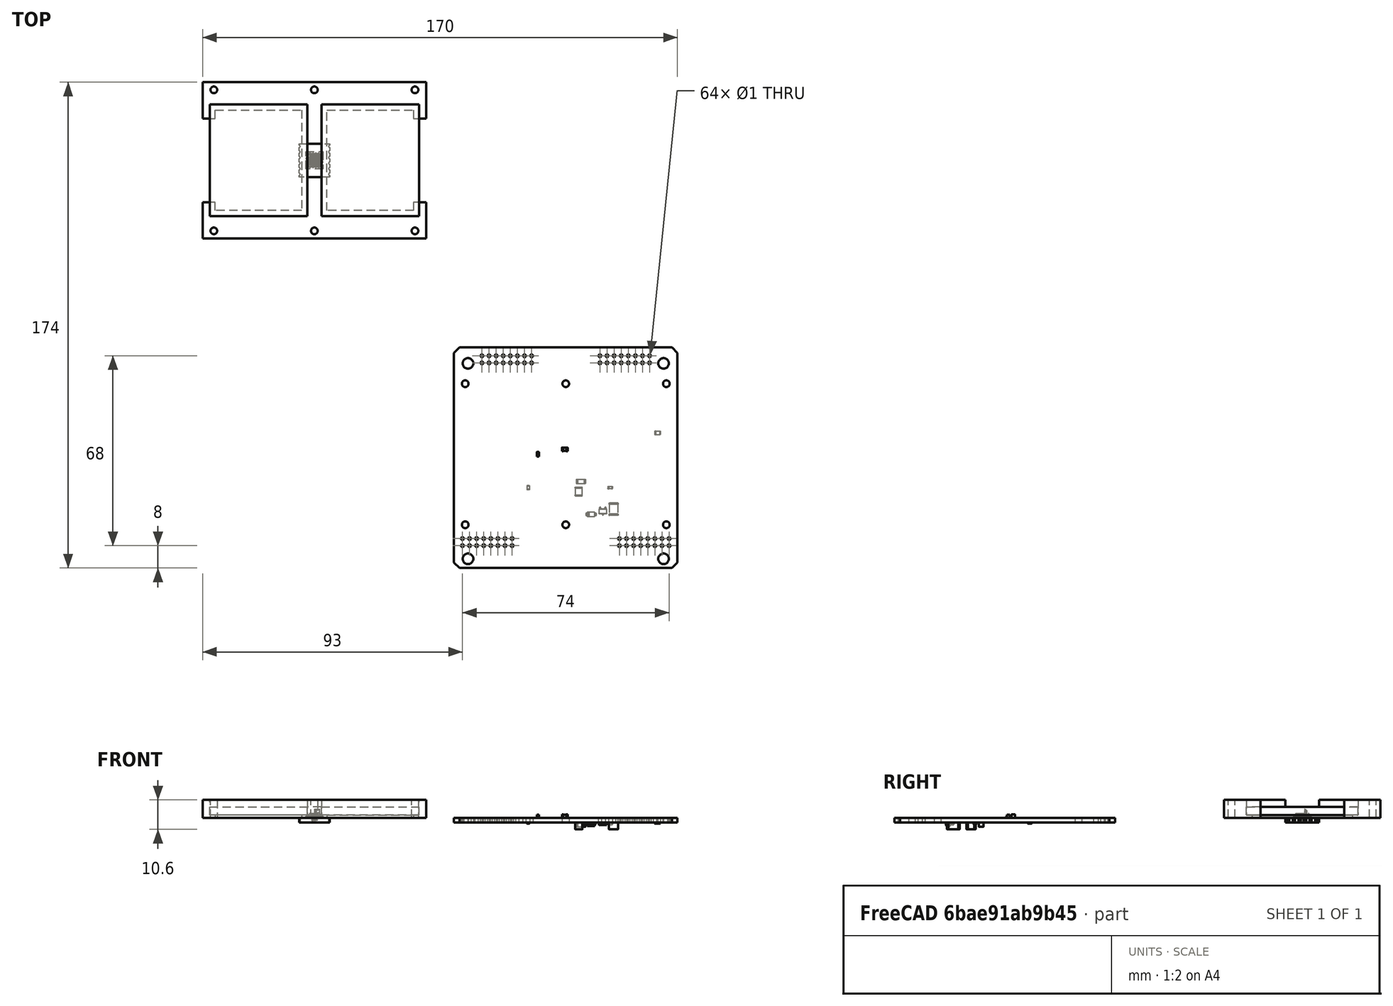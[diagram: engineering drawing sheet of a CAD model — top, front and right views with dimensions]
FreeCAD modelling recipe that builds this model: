
FCSTD DOCUMENT  (FreeCAD 0.21R33771 (Git))
Label: PlacaCarcasaV3
License: All rights reserved
LicenseURL: http://en.wikipedia.org/wiki/All_rights_reserved
objects: Part::Feature×268, App::Link×148, App::Part×28, PartDesign::CoordinateSystem×1, Sketcher::SketchObject×1
note: 270 computed .brp shape members not serialized (recipe doc carries the construction recipe); baked Part::Feature solids carry a one-line shape summary decoded from their .brp

FEATURE [PartDesign::CoordinateSystem] Local_CS_d980
  AttacherType = Attacher::AttachEngine3D
  MapMode = 2
  Support = -> [X_Axis001]
FEATURE [Part::Feature] Pcb_d980
  shape: bbox 80 x 79 x 1.6 mm, 84 faces (baked)
FEATURE [Sketcher::SketchObject] PCB_Sketch_d980
  FullyConstrained = false
  sketch-geometry (12):
    g0: LineSegment StartX=52 StartY=-146 StartZ=0 EndX=50 EndY=-144 EndZ=0
    g1: LineSegment StartX=50 StartY=-69 StartZ=0 EndX=52 EndY=-67 EndZ=0
    g2: LineSegment StartX=50 StartY=-144 StartZ=0 EndX=50 EndY=-69 EndZ=0
    g3: LineSegment StartX=52 StartY=-67 StartZ=0 EndX=128 EndY=-67 EndZ=0
    g4: LineSegment StartX=128 StartY=-146 StartZ=0 EndX=52 EndY=-146 EndZ=0
    g5: LineSegment StartX=128 StartY=-67 StartZ=0 EndX=130 EndY=-69 EndZ=0
    g6: LineSegment StartX=130 StartY=-69 StartZ=0 EndX=130 EndY=-144 EndZ=0
    g7: LineSegment StartX=130 StartY=-144 StartZ=0 EndX=128 EndY=-146 EndZ=0
    g8: Circle CenterX=125 CenterY=-142.7 CenterZ=0 NormalX=0 NormalY=0 NormalZ=1 AngleXU=0 Radius=1.9
    g9: Circle CenterX=55 CenterY=-72.7 CenterZ=0 NormalX=0 NormalY=0 NormalZ=1 AngleXU=0 Radius=1.9
    g10: Circle CenterX=55 CenterY=-142.7 CenterZ=0 NormalX=0 NormalY=0 NormalZ=1 AngleXU=0 Radius=1.9
    g11: Circle CenterX=125 CenterY=-72.7 CenterZ=0 NormalX=0 NormalY=0 NormalZ=1 AngleXU=0 Radius=1.9
  constraints (8):
    c: Coincident(g0,g2)
    c: Coincident(g1,g2)
    c: Coincident(g0,g4)
    c: Coincident(g1,g3)
    c: Coincident(g4,g7)
    c: Coincident(g3,g5)
    c: Coincident(g6,g7)
    c: Coincident(g5,g6)
FEATURE [Part::Feature] Part__Feature  label="BODY-SOT"
  Placement = pos=(0,0,0.9) rot=(0.57735,-0.57735,-0.57735;2.0944rad)
  shape: bbox 1.6 x 2.9 x 1.1 mm, 42 faces (baked)
FEATURE [Part::Feature] Part__Feature001  label="LEAD-SOT"
  Placement = pos=(-0.939537,-0.95,0.25) rot=(0.57735,-0.57735,-0.57735;2.0944rad)
  shape: bbox 0.6 x 0.4 x 0.9 mm, 14 faces (baked)
FEATURE [Part::Feature] Part__Feature002  label="LEAD-SOT001"
  Placement = pos=(-0.939537,0,0.25) rot=(0.57735,-0.57735,-0.57735;2.0944rad)
  shape: bbox 0.6 x 0.4 x 0.9 mm, 14 faces (baked)
FEATURE [Part::Feature] Part__Feature003  label="LEAD-SOT002"
  Placement = pos=(-0.939537,0.95,0.25) rot=(0.57735,-0.57735,-0.57735;2.0944rad)
  shape: bbox 0.6 x 0.4 x 0.9 mm, 14 faces (baked)
FEATURE [Part::Feature] Part__Feature004  label="LEAD-SOT003"
  Placement = pos=(0.939537,-0.95,0.25) rot=(0.57735,0.57735,0.57735;2.0944rad)
  shape: bbox 0.6 x 0.4 x 0.9 mm, 14 faces (baked)
FEATURE [Part::Feature] Part__Feature005  label="LEAD-SOT004"
  Placement = pos=(0.939537,0,0.25) rot=(0.57735,0.57735,0.57735;2.0944rad)
  shape: bbox 0.6 x 0.4 x 0.9 mm, 14 faces (baked)
FEATURE [Part::Feature] Part__Feature006  label="LEAD-SOT005"
  Placement = pos=(0.939537,0.95,0.25) rot=(0.57735,0.57735,0.57735;2.0944rad)
  shape: bbox 0.6 x 0.4 x 0.9 mm, 14 faces (baked)
FEATURE [App::Part] DBV0006A_ASM  label="07_SensorTemperatura.kicad_sch_DBV0006A_ASM_bef77850255a"
  Group = -> [Part__Feature,Part__Feature001,Part__Feature002,Part__Feature003,Part__Feature004,Part__Feature005,Part__Feature006]
  Origin = -> Origin008
  Placement = pos=(89.6348,-106.35,0) rot=(0,0,1;3.14159rad)
FEATURE [Part::Feature] Shape  label="06_PlacasSiPM.kicad_sch_LED_0603_1608Metric_667c60cf1737"
  Placement = pos=(80,-105.25,0) rot=(0,0,-1;1.5708rad)
  shape: bbox 0.8 x 1.6 x 1.1 mm, 50 faces (baked)
FEATURE [Part::Feature] Shape001  label="07_SensorTemperatura.kicad_sch_C_0805_2012Metric_4f3bec8a4ad3"
  Placement = pos=(89.65,-103.5,0) rot=(0,0,1;0rad)
  shape: bbox 2 x 1.25 x 1.25 mm, 28 faces (baked)
FEATURE [Part::Feature] Part__Feature007  label="Cuerpo"
  shape: bbox 80 x 56 x 6.5 mm, 44 faces (baked)
FEATURE [Part::Feature] Part__Feature008  label="Extrude"
  Placement = pos=(20,0,1) rot=(0,0,1;0rad)
  shape: bbox 35 x 40 x 3 mm, 6 faces (baked)
FEATURE [Part::Feature] Part__Feature009  label="Extrude001"
  Placement = pos=(-20,0,1) rot=(0,0,1;0rad)
  shape: bbox 35 x 40 x 3 mm, 6 faces (baked)
FEATURE [App::Part] CarcasaV3  label="06_PlacasSiPM.kicad_sch_CarcasaV3_ad8b2182f1ab"
  Group = -> [Part__Feature007,Part__Feature008,Part__Feature009]
  Origin = -> Origin009
  Placement = pos=(90,-105.25,6.5) rot=(1,0,0;3.14159rad)
FEATURE [App::Link] _6_PlacasSiPM_kicad_sch_LED_0603_1608Metric_667c60cf1737_ln_  label="06_PlacasSiPM.kicad_sch_PlacasSiPM.kicad_sch_LED_0603_1608Metric_7981f1ddc297"
  LinkPlacement = pos=(100,-105.25,0) rot=(0,0,-1;1.5708rad)
  LinkedObject = -> Shape
  Placement = pos=(100,-105.25,0) rot=(0,0,-1;1.5708rad)
FEATURE [Part::Feature] Part__Feature010  label="Pcb_1cf2"
  Placement = pos=(-150.5,123,0) rot=(0,0,1;0rad)
  shape: bbox 11 x 12 x 1.6 mm, 36 faces (baked)
FEATURE [Part::Feature] Part__Feature011  label="topPads_1cf2_cut"
  Placement = pos=(0,0,0.02) rot=(0,0,1;0rad)
  shape: bbox 0.675 x 1.35 x 2e-07 mm, 1 faces, 0 solids (baked)
FEATURE [Part::Feature] Part__Feature012  label="topPads_1cf2_cut001"
  Placement = pos=(0,0,0.02) rot=(0,0,1;0rad)
  shape: bbox 0.675 x 1.35 x 2e-07 mm, 1 faces, 0 solids (baked)
FEATURE [Part::Feature] Part__Feature013  label="topPads_1cf2_cut002"
  Placement = pos=(0,0,0.02) rot=(0,0,1;0rad)
  shape: bbox 0.675 x 1.35 x 2e-07 mm, 1 faces, 0 solids (baked)
FEATURE [Part::Feature] Part__Feature014  label="topPads_1cf2_cut003"
  Placement = pos=(0,0,0.02) rot=(0,0,1;0rad)
  shape: bbox 0.675 x 1.35 x 2e-07 mm, 1 faces, 0 solids (baked)
FEATURE [Part::Feature] Part__Feature015  label="topPads_1cf2_cut004"
  Placement = pos=(0,0,0.02) rot=(0,0,1;0rad)
  shape: bbox 0.675 x 1.35 x 2e-07 mm, 1 faces, 0 solids (baked)
FEATURE [Part::Feature] Part__Feature016  label="topPads_1cf2_cut005"
  Placement = pos=(0,0,0.02) rot=(0,0,1;0rad)
  shape: bbox 0.675 x 1.35 x 2e-07 mm, 1 faces, 0 solids (baked)
FEATURE [Part::Feature] Part__Feature017  label="topPads_1cf2_cut006"
  Placement = pos=(0,0,0.02) rot=(0,0,1;0rad)
  shape: bbox 0.675 x 1.35 x 2e-07 mm, 1 faces, 0 solids (baked)
FEATURE [Part::Feature] Part__Feature018  label="topPads_1cf2_cut007"
  Placement = pos=(0,0,0.02) rot=(0,0,1;0rad)
  shape: bbox 0.675 x 1.35 x 2e-07 mm, 1 faces, 0 solids (baked)
FEATURE [Part::Feature] Part__Feature019  label="topPads_1cf2_cut008"
  Placement = pos=(0,0,0.02) rot=(0,0,1;0rad)
  shape: bbox 0.675 x 1.35 x 2e-07 mm, 1 faces, 0 solids (baked)
FEATURE [Part::Feature] Part__Feature020  label="topPads_1cf2_cut009"
  Placement = pos=(0,0,0.02) rot=(0,0,1;0rad)
  shape: bbox 0.675 x 1.35 x 2e-07 mm, 1 faces, 0 solids (baked)
FEATURE [Part::Feature] Part__Feature021  label="topPads_1cf2_cut010"
  Placement = pos=(0,0,0.02) rot=(0,0,1;0rad)
  shape: bbox 0.675 x 1.35 x 2e-07 mm, 1 faces, 0 solids (baked)
FEATURE [Part::Feature] Part__Feature022  label="topPads_1cf2_cut011"
  Placement = pos=(0,0,0.02) rot=(0,0,1;0rad)
  shape: bbox 0.675 x 1.35 x 2e-07 mm, 1 faces, 0 solids (baked)
FEATURE [Part::Feature] Part__Feature023  label="topPads_1cf2_cut012"
  Placement = pos=(0,0,0.02) rot=(0,0,1;0rad)
  shape: bbox 0.6 x 0.6 x 2e-07 mm, 1 faces, 0 solids (baked)
FEATURE [Part::Feature] Part__Feature024  label="topPads_1cf2_cut013"
  Placement = pos=(0,0,0.02) rot=(0,0,1;0rad)
  shape: bbox 0.6 x 0.6 x 2e-07 mm, 1 faces, 0 solids (baked)
FEATURE [Part::Feature] Part__Feature025  label="topPads_1cf2_cut014"
  Placement = pos=(0,0,0.02) rot=(0,0,1;0rad)
  shape: bbox 0.6 x 0.6 x 2e-07 mm, 1 faces, 0 solids (baked)
FEATURE [Part::Feature] Part__Feature026  label="topPads_1cf2_cut015"
  Placement = pos=(0,0,0.02) rot=(0,0,1;0rad)
  shape: bbox 0.6 x 0.6 x 2e-07 mm, 1 faces, 0 solids (baked)
FEATURE [Part::Feature] Part__Feature027  label="topPads_1cf2_cut016"
  Placement = pos=(0,0,0.02) rot=(0,0,1;0rad)
  shape: bbox 0.6 x 0.6 x 2e-07 mm, 1 faces, 0 solids (baked)
FEATURE [Part::Feature] Part__Feature028  label="topPads_1cf2_cut017"
  Placement = pos=(0,0,0.02) rot=(0,0,1;0rad)
  shape: bbox 0.6 x 0.6 x 2e-07 mm, 1 faces, 0 solids (baked)
FEATURE [Part::Feature] Part__Feature029  label="topPads_1cf2_cut018"
  Placement = pos=(0,0,0.02) rot=(0,0,1;0rad)
  shape: bbox 0.2032 x 0.2032 x 2e-07 mm, 1 faces, 0 solids (baked)
FEATURE [Part::Feature] Part__Feature030  label="topPads_1cf2_cut019"
  Placement = pos=(0,0,0.02) rot=(0,0,1;0rad)
  shape: bbox 0.2032 x 0.2032 x 2e-07 mm, 1 faces, 0 solids (baked)
FEATURE [Part::Feature] Part__Feature031  label="topPads_1cf2_cut020"
  Placement = pos=(0,0,0.02) rot=(0,0,1;0rad)
  shape: bbox 0.2032 x 0.2032 x 2e-07 mm, 1 faces, 0 solids (baked)
FEATURE [Part::Feature] Part__Feature032  label="topPads_1cf2_cut021"
  Placement = pos=(0,0,0.02) rot=(0,0,1;0rad)
  shape: bbox 0.2032 x 0.2032 x 2e-07 mm, 1 faces, 0 solids (baked)
FEATURE [Part::Feature] Part__Feature033  label="topPads_1cf2_cut022"
  Placement = pos=(0,0,0.02) rot=(0,0,1;0rad)
  shape: bbox 0.2032 x 0.2032 x 2e-07 mm, 1 faces, 0 solids (baked)
FEATURE [Part::Feature] Part__Feature034  label="topPads_1cf2_cut023"
  Placement = pos=(0,0,0.02) rot=(0,0,1;0rad)
  shape: bbox 0.2032 x 0.2032 x 2e-07 mm, 1 faces, 0 solids (baked)
FEATURE [Part::Feature] Part__Feature035  label="topPads_1cf2_cut024"
  Placement = pos=(0,0,0.02) rot=(0,0,1;0rad)
  shape: bbox 0.2032 x 0.2032 x 2e-07 mm, 1 faces, 0 solids (baked)
FEATURE [Part::Feature] Part__Feature036  label="topPads_1cf2_cut025"
  Placement = pos=(0,0,0.02) rot=(0,0,1;0rad)
  shape: bbox 0.2032 x 0.2032 x 2e-07 mm, 1 faces, 0 solids (baked)
FEATURE [Part::Feature] Part__Feature037  label="topPads_1cf2_cut026"
  Placement = pos=(0,0,0.02) rot=(0,0,1;0rad)
  shape: bbox 0.2032 x 0.2032 x 2e-07 mm, 1 faces, 0 solids (baked)
FEATURE [Part::Feature] Part__Feature038  label="topPads_1cf2_cut027"
  Placement = pos=(0,0,0.02) rot=(0,0,1;0rad)
  shape: bbox 0.2032 x 0.2032 x 2e-07 mm, 1 faces, 0 solids (baked)
FEATURE [Part::Feature] Part__Feature039  label="topPads_1cf2_cut028"
  Placement = pos=(0,0,0.02) rot=(0,0,1;0rad)
  shape: bbox 0.2032 x 0.2032 x 2e-07 mm, 1 faces, 0 solids (baked)
FEATURE [Part::Feature] Part__Feature040  label="topPads_1cf2_cut029"
  Placement = pos=(0,0,0.02) rot=(0,0,1;0rad)
  shape: bbox 0.2032 x 0.2032 x 2e-07 mm, 1 faces, 0 solids (baked)
FEATURE [Part::Feature] Part__Feature041  label="topPads_1cf2_cut030"
  Placement = pos=(0,0,0.02) rot=(0,0,1;0rad)
  shape: bbox 0.2032 x 0.2032 x 2e-07 mm, 1 faces, 0 solids (baked)
FEATURE [Part::Feature] Part__Feature042  label="topPads_1cf2_cut031"
  Placement = pos=(0,0,0.02) rot=(0,0,1;0rad)
  shape: bbox 0.2032 x 0.2032 x 2e-07 mm, 1 faces, 0 solids (baked)
FEATURE [Part::Feature] Part__Feature043  label="topPads_1cf2_cut032"
  Placement = pos=(0,0,0.02) rot=(0,0,1;0rad)
  shape: bbox 0.2032 x 0.2032 x 2e-07 mm, 1 faces, 0 solids (baked)
FEATURE [Part::Feature] Part__Feature044  label="topPads_1cf2_cut033"
  Placement = pos=(0,0,0.02) rot=(0,0,1;0rad)
  shape: bbox 0.2032 x 0.2032 x 2e-07 mm, 1 faces, 0 solids (baked)
FEATURE [Part::Feature] Part__Feature045  label="topPads_1cf2_cut034"
  Placement = pos=(0,0,0.02) rot=(0,0,1;0rad)
  shape: bbox 0.2032 x 0.2032 x 2e-07 mm, 1 faces, 0 solids (baked)
FEATURE [Part::Feature] Part__Feature046  label="topPads_1cf2_cut035"
  Placement = pos=(0,0,0.02) rot=(0,0,1;0rad)
  shape: bbox 0.2032 x 0.2032 x 2e-07 mm, 1 faces, 0 solids (baked)
FEATURE [Part::Feature] Part__Feature047  label="topPads_1cf2_cut036"
  Placement = pos=(0,0,0.02) rot=(0,0,1;0rad)
  shape: bbox 0.2032 x 0.2032 x 2e-07 mm, 1 faces, 0 solids (baked)
FEATURE [Part::Feature] Part__Feature048  label="topPads_1cf2_cut037"
  Placement = pos=(0,0,0.02) rot=(0,0,1;0rad)
  shape: bbox 0.2032 x 0.2032 x 2e-07 mm, 1 faces, 0 solids (baked)
FEATURE [Part::Feature] Part__Feature049  label="topPads_1cf2_cut038"
  Placement = pos=(0,0,0.02) rot=(0,0,1;0rad)
  shape: bbox 0.2032 x 0.2032 x 2e-07 mm, 1 faces, 0 solids (baked)
FEATURE [Part::Feature] Part__Feature050  label="topPads_1cf2_cut039"
  Placement = pos=(0,0,0.02) rot=(0,0,1;0rad)
  shape: bbox 0.2032 x 0.2032 x 2e-07 mm, 1 faces, 0 solids (baked)
FEATURE [Part::Feature] Part__Feature051  label="topPads_1cf2_cut040"
  Placement = pos=(0,0,0.02) rot=(0,0,1;0rad)
  shape: bbox 0.2032 x 0.2032 x 2e-07 mm, 1 faces, 0 solids (baked)
FEATURE [Part::Feature] Part__Feature052  label="topPads_1cf2_cut041"
  Placement = pos=(0,0,0.02) rot=(0,0,1;0rad)
  shape: bbox 0.2032 x 0.2032 x 2e-07 mm, 1 faces, 0 solids (baked)
FEATURE [Part::Feature] Part__Feature053  label="topPads_1cf2_cut042"
  Placement = pos=(0,0,0.02) rot=(0,0,1;0rad)
  shape: bbox 0.2032 x 0.2032 x 2e-07 mm, 1 faces, 0 solids (baked)
FEATURE [Part::Feature] Part__Feature054  label="topPads_1cf2_cut043"
  Placement = pos=(0,0,0.02) rot=(0,0,1;0rad)
  shape: bbox 0.2032 x 0.2032 x 2e-07 mm, 1 faces, 0 solids (baked)
FEATURE [Part::Feature] Part__Feature055  label="topPads_1cf2_cut044"
  Placement = pos=(0,0,0.02) rot=(0,0,1;0rad)
  shape: bbox 0.2032 x 0.2032 x 2e-07 mm, 1 faces, 0 solids (baked)
FEATURE [Part::Feature] Part__Feature056  label="topPads_1cf2_cut045"
  Placement = pos=(0,0,0.02) rot=(0,0,1;0rad)
  shape: bbox 0.2032 x 0.2032 x 2e-07 mm, 1 faces, 0 solids (baked)
FEATURE [Part::Feature] Part__Feature057  label="topPads_1cf2_cut046"
  Placement = pos=(0,0,0.02) rot=(0,0,1;0rad)
  shape: bbox 0.2032 x 0.2032 x 2e-07 mm, 1 faces, 0 solids (baked)
FEATURE [Part::Feature] Part__Feature058  label="topPads_1cf2_cut047"
  Placement = pos=(0,0,0.02) rot=(0,0,1;0rad)
  shape: bbox 0.2032 x 0.2032 x 2e-07 mm, 1 faces, 0 solids (baked)
FEATURE [Part::Feature] Part__Feature059  label="topPads_1cf2_cut048"
  Placement = pos=(0,0,0.02) rot=(0,0,1;0rad)
  shape: bbox 0.2032 x 0.2032 x 2e-07 mm, 1 faces, 0 solids (baked)
FEATURE [Part::Feature] Part__Feature060  label="topPads_1cf2_cut049"
  Placement = pos=(0,0,0.02) rot=(0,0,1;0rad)
  shape: bbox 0.2032 x 0.2032 x 2e-07 mm, 1 faces, 0 solids (baked)
FEATURE [Part::Feature] Part__Feature061  label="topPads_1cf2_cut050"
  Placement = pos=(0,0,0.02) rot=(0,0,1;0rad)
  shape: bbox 0.2032 x 0.2032 x 2e-07 mm, 1 faces, 0 solids (baked)
FEATURE [Part::Feature] Part__Feature062  label="topPads_1cf2_cut051"
  Placement = pos=(0,0,0.02) rot=(0,0,1;0rad)
  shape: bbox 0.2032 x 0.2032 x 2e-07 mm, 1 faces, 0 solids (baked)
FEATURE [Part::Feature] Part__Feature063  label="topPads_1cf2_cut052"
  Placement = pos=(0,0,0.02) rot=(0,0,1;0rad)
  shape: bbox 0.2032 x 0.2032 x 2e-07 mm, 1 faces, 0 solids (baked)
FEATURE [Part::Feature] Part__Feature064  label="topPads_1cf2_cut053"
  Placement = pos=(0,0,0.02) rot=(0,0,1;0rad)
  shape: bbox 0.2032 x 0.2032 x 2e-07 mm, 1 faces, 0 solids (baked)
FEATURE [App::Part] topPads_1cf2_cut  label="topPads_1cf2_cut054"
  Group = -> [Part__Feature011,Part__Feature012,Part__Feature013,Part__Feature014,Part__Feature015,Part__Feature016,Part__Feature017,Part__Feature018,Part__Feature019,Part__Feature020,Part__Feature021,Part__Feature022,Part__Feature023,Part__Feature024,Part__Feature025,Part__Feature026,Part__Feature027,Part__Feature028,Part__Feature029,Part__Feature030,Part__Feature031,Part__Feature032,Part__Feature033,+31 more]
  Origin = -> Origin010
FEATURE [Part::Feature] Part__Feature065  label="topTracks_1cf2"
  Placement = pos=(-150.5,123,0.01) rot=(0,0,1;0rad)
  shape: bbox 0.8 x 2.3 x 2e-07 mm, 1 faces, 0 solids (baked)
FEATURE [Part::Feature] Part__Feature066  label="topTracks_1cf003"
  Placement = pos=(-150.5,123,0.01) rot=(0,0,1;0rad)
  shape: bbox 1.492 x 0.9917 x 2e-07 mm, 1 faces, 0 solids (baked)
FEATURE [Part::Feature] Part__Feature067  label="topTracks_1cf004"
  Placement = pos=(-150.5,123,0.01) rot=(0,0,1;0rad)
  shape: bbox 1.492 x 0.9917 x 2e-07 mm, 1 faces, 0 solids (baked)
FEATURE [Part::Feature] Part__Feature068  label="topTracks_1cf005"
  Placement = pos=(-150.5,123,0.01) rot=(0,0,1;0rad)
  shape: bbox 0.6917 x 1.592 x 2e-07 mm, 1 faces, 0 solids (baked)
FEATURE [Part::Feature] Part__Feature069  label="topTracks_1cf006"
  Placement = pos=(-150.5,123,0.01) rot=(0,0,1;0rad)
  shape: bbox 1.492 x 0.5917 x 2e-07 mm, 1 faces, 0 solids (baked)
FEATURE [Part::Feature] Part__Feature070  label="topTracks_1cf007"
  Placement = pos=(-150.5,123,0.01) rot=(0,0,1;0rad)
  shape: bbox 1.492 x 0.5917 x 2e-07 mm, 1 faces, 0 solids (baked)
FEATURE [Part::Feature] Part__Feature071  label="topTracks_1cf008"
  Placement = pos=(-150.5,123,0.01) rot=(0,0,1;0rad)
  shape: bbox 0.1969 x 0.1969 x 2e-07 mm, 1 faces, 0 solids (baked)
FEATURE [App::Part] topTracks_1cf2  label="topTracks_1cf009"
  Group = -> [Part__Feature065,Part__Feature066,Part__Feature067,Part__Feature068,Part__Feature069,Part__Feature070,Part__Feature071]
  Origin = -> Origin011
FEATURE [Part::Feature] Part__Feature072  label="topZones_1cf2"
  Placement = pos=(-150.5,123,0.01) rot=(0,0,1;0rad)
  shape: bbox 10.7 x 12.05 x 2e-07 mm, 1 faces, 0 solids (baked)
FEATURE [Part::Feature] Part__Feature073  label="botPads_1cf2_cut"
  Placement = pos=(0,0,-1.62) rot=(0,0,1;0rad)
  shape: bbox 0.675 x 1.35 x 2e-07 mm, 1 faces, 0 solids (baked)
FEATURE [Part::Feature] Part__Feature074  label="botPads_1cf2_cut001"
  Placement = pos=(0,0,-1.62) rot=(0,0,1;0rad)
  shape: bbox 0.675 x 1.35 x 2e-07 mm, 1 faces, 0 solids (baked)
FEATURE [Part::Feature] Part__Feature075  label="botPads_1cf2_cut002"
  Placement = pos=(0,0,-1.62) rot=(0,0,1;0rad)
  shape: bbox 0.675 x 1.35 x 2e-07 mm, 1 faces, 0 solids (baked)
FEATURE [Part::Feature] Part__Feature076  label="botPads_1cf2_cut003"
  Placement = pos=(0,0,-1.62) rot=(0,0,1;0rad)
  shape: bbox 0.675 x 1.35 x 2e-07 mm, 1 faces, 0 solids (baked)
FEATURE [Part::Feature] Part__Feature077  label="botPads_1cf2_cut004"
  Placement = pos=(0,0,-1.62) rot=(0,0,1;0rad)
  shape: bbox 0.675 x 1.35 x 2e-07 mm, 1 faces, 0 solids (baked)
FEATURE [Part::Feature] Part__Feature078  label="botPads_1cf2_cut005"
  Placement = pos=(0,0,-1.62) rot=(0,0,1;0rad)
  shape: bbox 0.675 x 1.35 x 2e-07 mm, 1 faces, 0 solids (baked)
FEATURE [Part::Feature] Part__Feature079  label="botPads_1cf2_cut006"
  Placement = pos=(0,0,-1.62) rot=(0,0,1;0rad)
  shape: bbox 0.675 x 1.35 x 2e-07 mm, 1 faces, 0 solids (baked)
FEATURE [Part::Feature] Part__Feature080  label="botPads_1cf2_cut007"
  Placement = pos=(0,0,-1.62) rot=(0,0,1;0rad)
  shape: bbox 0.675 x 1.35 x 2e-07 mm, 1 faces, 0 solids (baked)
FEATURE [Part::Feature] Part__Feature081  label="botPads_1cf2_cut008"
  Placement = pos=(0,0,-1.62) rot=(0,0,1;0rad)
  shape: bbox 0.675 x 1.35 x 2e-07 mm, 1 faces, 0 solids (baked)
FEATURE [Part::Feature] Part__Feature082  label="botPads_1cf2_cut009"
  Placement = pos=(0,0,-1.62) rot=(0,0,1;0rad)
  shape: bbox 0.675 x 1.35 x 2e-07 mm, 1 faces, 0 solids (baked)
FEATURE [Part::Feature] Part__Feature083  label="botPads_1cf2_cut010"
  Placement = pos=(0,0,-1.62) rot=(0,0,1;0rad)
  shape: bbox 0.675 x 1.35 x 2e-07 mm, 1 faces, 0 solids (baked)
FEATURE [Part::Feature] Part__Feature084  label="botPads_1cf2_cut011"
  Placement = pos=(0,0,-1.62) rot=(0,0,1;0rad)
  shape: bbox 0.675 x 1.35 x 2e-07 mm, 1 faces, 0 solids (baked)
FEATURE [Part::Feature] Part__Feature085  label="botPads_1cf2_cut012"
  Placement = pos=(0,0,-1.62) rot=(0,0,1;0rad)
  shape: bbox 0.6 x 0.6 x 2e-07 mm, 1 faces, 0 solids (baked)
FEATURE [Part::Feature] Part__Feature086  label="botPads_1cf2_cut013"
  Placement = pos=(0,0,-1.62) rot=(0,0,1;0rad)
  shape: bbox 0.6 x 0.6 x 2e-07 mm, 1 faces, 0 solids (baked)
FEATURE [Part::Feature] Part__Feature087  label="botPads_1cf2_cut014"
  Placement = pos=(0,0,-1.62) rot=(0,0,1;0rad)
  shape: bbox 0.6 x 0.6 x 2e-07 mm, 1 faces, 0 solids (baked)
FEATURE [Part::Feature] Part__Feature088  label="botPads_1cf2_cut015"
  Placement = pos=(0,0,-1.62) rot=(0,0,1;0rad)
  shape: bbox 0.6 x 0.6 x 2e-07 mm, 1 faces, 0 solids (baked)
FEATURE [Part::Feature] Part__Feature089  label="botPads_1cf2_cut016"
  Placement = pos=(0,0,-1.62) rot=(0,0,1;0rad)
  shape: bbox 0.6 x 0.6 x 2e-07 mm, 1 faces, 0 solids (baked)
FEATURE [Part::Feature] Part__Feature090  label="botPads_1cf2_cut017"
  Placement = pos=(0,0,-1.62) rot=(0,0,1;0rad)
  shape: bbox 0.6 x 0.6 x 2e-07 mm, 1 faces, 0 solids (baked)
FEATURE [App::Part] botPads_1cf2_cut  label="botPads_1cf2_cut018"
  Group = -> [Part__Feature073,Part__Feature074,Part__Feature075,Part__Feature076,Part__Feature077,Part__Feature078,Part__Feature079,Part__Feature080,Part__Feature081,Part__Feature082,Part__Feature083,Part__Feature084,Part__Feature085,Part__Feature086,Part__Feature087,Part__Feature088,Part__Feature089,Part__Feature090]
  Origin = -> Origin012
FEATURE [Part::Feature] Part__Feature091  label="botTracks_1cf2"
  Placement = pos=(-150.5,123,-1.61) rot=(0,0,1;0rad)
  shape: bbox 9.113 x 5.6 x 2e-07 mm, 1 faces, 0 solids (baked)
FEATURE [Part::Feature] Part__Feature092  label="botTracks_1cf003"
  Placement = pos=(-150.5,123,-1.61) rot=(0,0,1;0rad)
  shape: bbox 1.297 x 3.297 x 2e-07 mm, 1 faces, 0 solids (baked)
FEATURE [App::Part] botTracks_1cf2  label="botTracks_1cf004"
  Group = -> [Part__Feature091,Part__Feature092]
  Origin = -> Origin013
FEATURE [App::Part] Board_Geoms_1cf2
  Group = -> [Part__Feature010,topPads_1cf2_cut,topTracks_1cf2,Part__Feature072,botPads_1cf2_cut,botTracks_1cf2]
  Origin = -> Origin014
FEATURE [Part::Feature] Part__Feature093  label="part"
  shape: bbox 0.254 x 0.254 x 0.254 mm, 1 faces (baked)
FEATURE [Part::Feature] Part__Feature094  label="part001"
  shape: bbox 0.254 x 0.254 x 0.254 mm, 1 faces (baked)
FEATURE [Part::Feature] Part__Feature095  label="part002"
  shape: bbox 0.254 x 0.254 x 0.254 mm, 1 faces (baked)
FEATURE [Part::Feature] Part__Feature096  label="part003"
  shape: bbox 0.254 x 0.254 x 0.254 mm, 1 faces (baked)
FEATURE [Part::Feature] Part__Feature097  label="part004"
  shape: bbox 0.254 x 0.254 x 0.254 mm, 1 faces (baked)
FEATURE [Part::Feature] Part__Feature098  label="part005"
  shape: bbox 0.254 x 0.254 x 0.254 mm, 1 faces (baked)
FEATURE [Part::Feature] Part__Feature099  label="part006"
  shape: bbox 0.254 x 0.254 x 0.254 mm, 1 faces (baked)
FEATURE [Part::Feature] Part__Feature100  label="part007"
  shape: bbox 0.254 x 0.254 x 0.254 mm, 1 faces (baked)
FEATURE [Part::Feature] Part__Feature101  label="part008"
  shape: bbox 0.254 x 0.254 x 0.254 mm, 1 faces (baked)
FEATURE [Part::Feature] Part__Feature102  label="part009"
  shape: bbox 0.254 x 0.254 x 0.254 mm, 1 faces (baked)
FEATURE [Part::Feature] Part__Feature103  label="part010"
  shape: bbox 0.254 x 0.254 x 0.254 mm, 1 faces (baked)
FEATURE [Part::Feature] Part__Feature104  label="part011"
  shape: bbox 0.254 x 0.254 x 0.254 mm, 1 faces (baked)
FEATURE [Part::Feature] Part__Feature105  label="part012"
  shape: bbox 0.254 x 0.254 x 0.254 mm, 1 faces (baked)
FEATURE [Part::Feature] Part__Feature106  label="part013"
  shape: bbox 0.254 x 0.254 x 0.254 mm, 1 faces (baked)
FEATURE [Part::Feature] Part__Feature107  label="part014"
  shape: bbox 0.254 x 0.254 x 0.254 mm, 1 faces (baked)
FEATURE [Part::Feature] Part__Feature108  label="part015"
  shape: bbox 0.254 x 0.254 x 0.254 mm, 1 faces (baked)
FEATURE [Part::Feature] Part__Feature109  label="part016"
  shape: bbox 0.254 x 0.254 x 0.254 mm, 1 faces (baked)
FEATURE [Part::Feature] Part__Feature110  label="part017"
  shape: bbox 0.254 x 0.254 x 0.254 mm, 1 faces (baked)
FEATURE [Part::Feature] Part__Feature111  label="part018"
  shape: bbox 0.254 x 0.254 x 0.254 mm, 1 faces (baked)
FEATURE [Part::Feature] Part__Feature112  label="part019"
  shape: bbox 0.254 x 0.254 x 0.254 mm, 1 faces (baked)
FEATURE [Part::Feature] Part__Feature113  label="part020"
  shape: bbox 0.254 x 0.254 x 0.254 mm, 1 faces (baked)
FEATURE [Part::Feature] Part__Feature114  label="part021"
  shape: bbox 0.254 x 0.254 x 0.254 mm, 1 faces (baked)
FEATURE [Part::Feature] Part__Feature115  label="part022"
  shape: bbox 0.254 x 0.254 x 0.254 mm, 1 faces (baked)
FEATURE [Part::Feature] Part__Feature116  label="part023"
  shape: bbox 0.254 x 0.254 x 0.254 mm, 1 faces (baked)
FEATURE [Part::Feature] Part__Feature117  label="part024"
  shape: bbox 0.254 x 0.254 x 0.254 mm, 1 faces (baked)
FEATURE [Part::Feature] Part__Feature118  label="part025"
  shape: bbox 0.254 x 0.254 x 0.254 mm, 1 faces (baked)
FEATURE [Part::Feature] Part__Feature119  label="part026"
  shape: bbox 0.254 x 0.254 x 0.254 mm, 1 faces (baked)
FEATURE [Part::Feature] Part__Feature120  label="part027"
  shape: bbox 0.254 x 0.254 x 0.254 mm, 1 faces (baked)
FEATURE [Part::Feature] Part__Feature121  label="part028"
  shape: bbox 0.254 x 0.254 x 0.254 mm, 1 faces (baked)
FEATURE [Part::Feature] Part__Feature122  label="part029"
  shape: bbox 0.254 x 0.254 x 0.254 mm, 1 faces (baked)
FEATURE [Part::Feature] Part__Feature123  label="part030"
  shape: bbox 0.254 x 0.254 x 0.254 mm, 1 faces (baked)
FEATURE [Part::Feature] Part__Feature124  label="part031"
  shape: bbox 0.254 x 0.254 x 0.254 mm, 1 faces (baked)
FEATURE [Part::Feature] Part__Feature125  label="part032"
  shape: bbox 0.254 x 0.254 x 0.254 mm, 1 faces (baked)
FEATURE [Part::Feature] Part__Feature126  label="part033"
  shape: bbox 0.254 x 0.254 x 0.254 mm, 1 faces (baked)
FEATURE [Part::Feature] Part__Feature127  label="part034"
  shape: bbox 0.254 x 0.254 x 0.254 mm, 1 faces (baked)
FEATURE [Part::Feature] Part__Feature128  label="part035"
  shape: bbox 0.254 x 0.254 x 0.254 mm, 1 faces (baked)
FEATURE [Part::Feature] Part__Feature129  label="part036"
  shape: bbox 0.3086 x 0.3086 x 0.003 mm, 3 faces (baked)
FEATURE [Part::Feature] Part__Feature130  label="part037"
  shape: bbox 6.172 x 6.172 x 0.407 mm, 6 faces (baked)
FEATURE [App::Part] Placa_SiPM_kicad_sch_part038_7e5b207e7f31  label="Placa_SiPM.kicad_sch_part038_7e5b207e7f31"
  Group = -> [Part__Feature093,Part__Feature094,Part__Feature095,Part__Feature096,Part__Feature097,Part__Feature098,Part__Feature099,Part__Feature100,Part__Feature101,Part__Feature102,Part__Feature103,Part__Feature104,Part__Feature105,Part__Feature106,Part__Feature107,Part__Feature108,Part__Feature109,Part__Feature110,Part__Feature111,Part__Feature112,Part__Feature113,Part__Feature114,Part__Feature115,+15 more]
  Origin = -> Origin015
FEATURE [App::Part] Top_1cf2
  Group = -> [Placa_SiPM_kicad_sch_part038_7e5b207e7f31]
  Origin = -> Origin016
FEATURE [App::Part] Step_Models_1cf2
  Group = -> [Top_1cf2]
  Origin = -> Origin017
FEATURE [App::Part] Placa_SiPM  label="06_PlacasSiPM.kicad_sch_Placa_SiPM_8cd53adc4c3a"
  Group = -> [Board_Geoms_1cf2,Step_Models_1cf2]
  Origin = -> Origin018
  Placement = pos=(70,-105.25,1.6) rot=(0,0,1;0rad)
FEATURE [App::Link] _6_PlacasSiPM_kicad_sch_Placa_SiPM_8cd53adc4c3a_ln_  label="06_PlacasSiPM.kicad_sch_PlacasSiPM.kicad_sch_Placa_SiPM_0cbb51f1506e"
  LinkPlacement = pos=(110,-105.25,1.6) rot=(0,0,1;0rad)
  LinkedObject = -> Placa_SiPM
  Placement = pos=(110,-105.25,1.6) rot=(0,0,1;0rad)
FEATURE [App::Part] Top_d980
  Group = -> [DBV0006A_ASM,Shape,Shape001,CarcasaV3,_6_PlacasSiPM_kicad_sch_LED_0603_1608Metric_667c60cf1737_ln_,Placa_SiPM,_6_PlacasSiPM_kicad_sch_Placa_SiPM_8cd53adc4c3a_ln_]
  Origin = -> Origin003
FEATURE [Part::Feature] Shape002  label="01_Polarizacion.kicad_sch_TSOT_23_32137845036f"
  Placement = pos=(103.275,-125.665,-1.6) rot=(0.707107,-0.707107,0;3.14159rad)
  shape: bbox 2.9 x 2.8 x 0.95 mm, 79 faces (baked)
FEATURE [Part::Feature] Shape003  label="04_GenVref.kicad_sch_R_0805_2012Metric_e7e7c0ed52a6"
  Placement = pos=(122.85,-97.568,-1.6) rot=(1,0,0;3.14159rad)
  shape: bbox 2 x 1.2 x 0.45 mm, 26 faces (baked)
FEATURE [Part::Feature] Shape004  label="01_Polarizacion.kicad_sch_R_0603_1608Metric_55dffa615082"
  Placement = pos=(76.525,-117.25,-1.6) rot=(0.707107,-0.707107,0;3.14159rad)
  shape: bbox 0.8 x 1.6 x 0.45 mm, 26 faces (baked)
FEATURE [App::Link] _4_GenVref_kicad_sch_R_0805_2012Metric_e7e7c0ed52a6_ln_  label="03_Comparación.kicad_sch_GenVref.kicad_sch_R_0805_2012Metric_dcaada17983d"
  LinkPlacement = pos=(93.45,-93.75,-1.6) rot=(0.707107,0.707107,0;3.14159rad)
  LinkedObject = -> Shape003
  Placement = pos=(93.45,-93.75,-1.6) rot=(0.707107,0.707107,0;3.14159rad)
FEATURE [Part::Feature] Part__Feature131  label="BODY_MUA08A"
  Placement = pos=(0,0,0.6897) rot=(0.57735,-0.57735,-0.57735;2.0944rad)
  shape: bbox 2.999 x 2.999 x 0.9985 mm, 46 faces (baked)
FEATURE [Part::Feature] Part__Feature132  label="LEAD_MUA08A"
  Placement = pos=(-1.9177,-0.97536,0.254) rot=(0.57735,-0.57735,-0.57735;2.0944rad)
  shape: bbox 0.9525 x 0.3048 x 0.6897 mm, 14 faces (baked)
FEATURE [Part::Feature] Part__Feature133  label="LEAD_MUA08A001"
  Placement = pos=(-1.9177,-0.32512,0.254) rot=(0.57735,-0.57735,-0.57735;2.0944rad)
  shape: bbox 0.9525 x 0.3048 x 0.6897 mm, 14 faces (baked)
FEATURE [Part::Feature] Part__Feature134  label="LEAD_MUA08A002"
  Placement = pos=(-1.9177,0.32512,0.254) rot=(0.57735,-0.57735,-0.57735;2.0944rad)
  shape: bbox 0.9525 x 0.3048 x 0.6897 mm, 14 faces (baked)
FEATURE [Part::Feature] Part__Feature135  label="LEAD_MUA08A003"
  Placement = pos=(-1.9177,0.97536,0.254) rot=(0.57735,-0.57735,-0.57735;2.0944rad)
  shape: bbox 0.9525 x 0.3048 x 0.6897 mm, 14 faces (baked)
FEATURE [Part::Feature] Part__Feature136  label="LEAD_MUA08A004"
  Placement = pos=(1.9177,-0.97536,0.254) rot=(0.57735,0.57735,0.57735;2.0944rad)
  shape: bbox 0.9525 x 0.3048 x 0.6897 mm, 14 faces (baked)
FEATURE [Part::Feature] Part__Feature137  label="LEAD_MUA08A005"
  Placement = pos=(1.9177,-0.32512,0.254) rot=(0.57735,0.57735,0.57735;2.0944rad)
  shape: bbox 0.9525 x 0.3048 x 0.6897 mm, 14 faces (baked)
FEATURE [Part::Feature] Part__Feature138  label="LEAD_MUA08A006"
  Placement = pos=(1.9177,0.32512,0.254) rot=(0.57735,0.57735,0.57735;2.0944rad)
  shape: bbox 0.9525 x 0.3048 x 0.6897 mm, 14 faces (baked)
FEATURE [Part::Feature] Part__Feature139  label="LEAD_MUA08A007"
  Placement = pos=(1.9177,0.97536,0.254) rot=(0.57735,0.57735,0.57735;2.0944rad)
  shape: bbox 0.9525 x 0.3048 x 0.6897 mm, 14 faces (baked)
FEATURE [App::Part] MUA08A_ASM  label="01_Polarizacion.kicad_sch_MUA08A_ASM_555f9891b5ac"
  Group = -> [Part__Feature131,Part__Feature132,Part__Feature133,Part__Feature134,Part__Feature135,Part__Feature136,Part__Feature137,Part__Feature138,Part__Feature139]
  Origin = -> Origin019
  Placement = pos=(78.8633,-134.025,-1.6) rot=(1,0,0;3.14159rad)
FEATURE [Part::Feature] Shape005  label="01_Polarizacion.kicad_sch_C_1206_3216Metric_f1471ee13c61"
  Placement = pos=(95.4,-114.975,-1.6) rot=(1,0,0;3.14159rad)
  shape: bbox 3.2 x 1.6 x 1.6 mm, 28 faces (baked)
FEATURE [App::Link] _7_SensorTemperatura_kicad_sch_C_0805_2012Metric_4f3bec8a4ad3_ln_  label="03_Comparación.kicad_sch_SensorTemperatura.kicad_sch_C_0805_2012Metric_bb25651ed259"
  LinkPlacement = pos=(87.15,-94.5217,-1.6) rot=(0.707107,-0.707107,0;3.14159rad)
  LinkedObject = -> Shape001
  Placement = pos=(87.15,-94.5217,-1.6) rot=(0.707107,-0.707107,0;3.14159rad)
FEATURE [App::Link] _4_GenVref_kicad_sch_R_0805_2012Metric_e7e7c0ed52a6_ln_001  label="01_Polarizacion.kicad_sch_GenVref.kicad_sch_R_0805_2012Metric_055e7035bca4"
  LinkPlacement = pos=(95.65,-133.1,-1.6) rot=(0,1,0;3.14159rad)
  LinkedObject = -> Shape003
  Placement = pos=(95.65,-133.1,-1.6) rot=(0,1,0;3.14159rad)
FEATURE [App::Link] _4_GenVref_kicad_sch_R_0805_2012Metric_e7e7c0ed52a6_ln_002  label="08_MedicionCorriente.kicad_sch_GenVref.kicad_sch_R_0805_2012Metric_8d90b72a5bf4"
  LinkPlacement = pos=(63.3147,-92.6719,-1.6) rot=(0.707107,-0.707107,0;3.14159rad)
  LinkedObject = -> Shape003
  Placement = pos=(63.3147,-92.6719,-1.6) rot=(0.707107,-0.707107,0;3.14159rad)
FEATURE [App::Link] _4_GenVref_kicad_sch_R_0805_2012Metric_e7e7c0ed52a6_ln_003  label="Placa_DetectorParticulas.kicad_sch_GenVref.kicad_sch_R_0805_2012Metric_d41f5b83ae95"
  LinkPlacement = pos=(92.3,-84.95,-1.6) rot=(0.707107,0.707107,0;3.14159rad)
  LinkedObject = -> Shape003
  Placement = pos=(92.3,-84.95,-1.6) rot=(0.707107,0.707107,0;3.14159rad)
FEATURE [App::Link] _7_SensorTemperatura_kicad_sch_C_0805_2012Metric_4f3bec8a4ad3_ln_001  label="01_Polarizacion.kicad_sch_SensorTemperatura.kicad_sch_C_0805_2012Metric_c7f56b1b11b2"
  LinkPlacement = pos=(101.8,-137.1,-1.6) rot=(1,0,0;3.14159rad)
  LinkedObject = -> Shape001
  Placement = pos=(101.8,-137.1,-1.6) rot=(1,0,0;3.14159rad)
FEATURE [Part::Feature] Shape006  label="01_Polarizacion.kicad_sch_D_SOD_123_c84daf4213db"
  Placement = pos=(99.025,-126.775,-1.6) rot=(1,0,0;3.14159rad)
  shape: bbox 3.8 x 1.6 x 1.25 mm, 67 faces (baked)
FEATURE [App::Link] _4_GenVref_kicad_sch_R_0805_2012Metric_e7e7c0ed52a6_ln_004  label="08_MedicionCorriente.kicad_sch_GenVref.kicad_sch_R_0805_2012Metric_9b7ff64fadd9"
  LinkPlacement = pos=(117.375,-91.2,-1.6) rot=(0.707107,0.707107,0;3.14159rad)
  LinkedObject = -> Shape003
  Placement = pos=(117.375,-91.2,-1.6) rot=(0.707107,0.707107,0;3.14159rad)
FEATURE [Part::Feature] Shape007  label="01_Polarizacion.kicad_sch_C_0603_1608Metric_c67edd4d6b6e"
  Placement = pos=(105.9,-117.175,-1.6) rot=(1,0,0;3.14159rad)
  shape: bbox 1.6 x 0.8 x 0.8 mm, 28 faces (baked)
FEATURE [App::Link] _7_SensorTemperatura_kicad_sch_C_0805_2012Metric_4f3bec8a4ad3_ln_002  label="02_Amplificacion.kicad_sch_SensorTemperatura.kicad_sch_C_0805_2012Metric_19082a8ab6bc"
  LinkPlacement = pos=(80.3003,-107.869,-1.6) rot=(0,1,0;3.14159rad)
  LinkedObject = -> Shape001
  Placement = pos=(80.3003,-107.869,-1.6) rot=(0,1,0;3.14159rad)
FEATURE [App::Link] _4_GenVref_kicad_sch_R_0805_2012Metric_e7e7c0ed52a6_ln_005  label="Placa_DetectorParticulas.kicad_sch_GenVref.kicad_sch_R_0805_2012Metric_88ffaab2a4e8"
  LinkPlacement = pos=(80.3,-91.1125,-1.6) rot=(0.707107,0.707107,0;3.14159rad)
  LinkedObject = -> Shape003
  Placement = pos=(80.3,-91.1125,-1.6) rot=(0.707107,0.707107,0;3.14159rad)
FEATURE [App::Link] _7_SensorTemperatura_kicad_sch_C_0805_2012Metric_4f3bec8a4ad3_ln_003  label="02_Amplificacion.kicad_sch_SensorTemperatura.kicad_sch_C_0805_2012Metric_e581be577117"
  LinkPlacement = pos=(102.6,-104.6,-1.6) rot=(0.707107,-0.707107,0;3.14159rad)
  LinkedObject = -> Shape001
  Placement = pos=(102.6,-104.6,-1.6) rot=(0.707107,-0.707107,0;3.14159rad)
FEATURE [Part::Feature] Part__Feature140  label="part038"
  shape: bbox 0.145 x 0.145 x 0.003 mm, 3 faces (baked)
FEATURE [Part::Feature] Part__Feature141  label="part039"
  shape: bbox 2.901 x 1.301 x 1.121 mm, 14 faces (baked)
FEATURE [Part::Feature] Part__Feature142  label="part040"
  shape: bbox 0.513 x 0.672 x 0.562 mm, 14 faces (baked)
FEATURE [Part::Feature] Part__Feature143  label="part041"
  shape: bbox 0.5111 x 0.6711 x 0.5611 mm, 14 faces (baked)
FEATURE [Part::Feature] Part__Feature144  label="part042"
  shape: bbox 0.5111 x 0.6711 x 0.5611 mm, 14 faces (baked)
FEATURE [App::Part] part  label="01_Polarizacion.kicad_sch_part043_50eeabfdbd3f"
  Group = -> [Part__Feature140,Part__Feature141,Part__Feature142,Part__Feature143,Part__Feature144]
  Origin = -> Origin020
  Placement = pos=(95.13,-136.093,-1.6) rot=(0.707107,-0.707107,0;3.14159rad)
FEATURE [App::Link] _4_GenVref_kicad_sch_R_0805_2012Metric_e7e7c0ed52a6_ln_006  label="04_GenVref.kicad_sch_GenVref.kicad_sch_R_0805_2012Metric_99ee876c09b5"
  LinkPlacement = pos=(57.2375,-118.35,-1.6) rot=(1,0,0;3.14159rad)
  LinkedObject = -> Shape003
  Placement = pos=(57.2375,-118.35,-1.6) rot=(1,0,0;3.14159rad)
FEATURE [App::Link] _4_GenVref_kicad_sch_R_0805_2012Metric_e7e7c0ed52a6_ln_007  label="02_Amplificacion.kicad_sch_GenVref.kicad_sch_R_0805_2012Metric_eb8a10d69283"
  LinkPlacement = pos=(80.3178,-101.789,-1.6) rot=(1,0,0;3.14159rad)
  LinkedObject = -> Shape003
  Placement = pos=(80.3178,-101.789,-1.6) rot=(1,0,0;3.14159rad)
FEATURE [App::Link] _7_SensorTemperatura_kicad_sch_C_0805_2012Metric_4f3bec8a4ad3_ln_004  label="03_Comparación.kicad_sch_SensorTemperatura.kicad_sch_C_0805_2012Metric_0c196a01d999"
  LinkPlacement = pos=(97.1717,-90.0717,-1.6) rot=(0.707107,-0.707107,0;3.14159rad)
  LinkedObject = -> Shape001
  Placement = pos=(97.1717,-90.0717,-1.6) rot=(0.707107,-0.707107,0;3.14159rad)
FEATURE [App::Link] _4_GenVref_kicad_sch_R_0805_2012Metric_e7e7c0ed52a6_ln_008  label="06_PlacasSiPM.kicad_sch_GenVref.kicad_sch_R_0805_2012Metric_111589959746"
  LinkPlacement = pos=(55.75,-87.2125,-1.6) rot=(0.707107,0.707107,0;3.14159rad)
  LinkedObject = -> Shape003
  Placement = pos=(55.75,-87.2125,-1.6) rot=(0.707107,0.707107,0;3.14159rad)
FEATURE [App::Link] _7_SensorTemperatura_kicad_sch_C_0805_2012Metric_4f3bec8a4ad3_ln_005  label="08_MedicionCorriente.kicad_sch_SensorTemperatura.kicad_sch_C_0805_2012Metric_3553cda95077"
  LinkPlacement = pos=(63.2647,-96.9594,-1.6) rot=(1,0,0;3.14159rad)
  LinkedObject = -> Shape001
  Placement = pos=(63.2647,-96.9594,-1.6) rot=(1,0,0;3.14159rad)
FEATURE [App::Link] _7_SensorTemperatura_kicad_sch_C_0805_2012Metric_4f3bec8a4ad3_ln_006  label="02_Amplificacion.kicad_sch_SensorTemperatura.kicad_sch_C_0805_2012Metric_72b3d80cd8ed"
  LinkPlacement = pos=(88.1003,-106.369,-1.6) rot=(0.707107,-0.707107,0;3.14159rad)
  LinkedObject = -> Shape001
  Placement = pos=(88.1003,-106.369,-1.6) rot=(0.707107,-0.707107,0;3.14159rad)
FEATURE [App::Link] _4_GenVref_kicad_sch_R_0805_2012Metric_e7e7c0ed52a6_ln_009  label="01_Polarizacion.kicad_sch_GenVref.kicad_sch_R_0805_2012Metric_c6fd1157d9b8"
  LinkPlacement = pos=(91.45,-118.062,-1.6) rot=(0.707107,-0.707107,0;3.14159rad)
  LinkedObject = -> Shape003
  Placement = pos=(91.45,-118.062,-1.6) rot=(0.707107,-0.707107,0;3.14159rad)
FEATURE [Part::Feature] Shape008  label="01_Polarizacion.kicad_sch_L_1210_3225Metric_350fa5c3db90"
  Placement = pos=(94.675,-118.575,-1.6) rot=(0.707107,0.707107,0;3.14159rad)
  shape: bbox 2.5 x 3.2 x 2.5 mm, 28 faces (baked)
FEATURE [App::Link] _4_GenVref_kicad_sch_R_0805_2012Metric_e7e7c0ed52a6_ln_010  label="01_Polarizacion.kicad_sch_GenVref.kicad_sch_R_0805_2012Metric_a1759b9fb863"
  LinkPlacement = pos=(66.9,-122.8,-1.6) rot=(1,0,0;3.14159rad)
  LinkedObject = -> Shape003
  Placement = pos=(66.9,-122.8,-1.6) rot=(1,0,0;3.14159rad)
FEATURE [Part::Feature] Part__Feature145  label="part043"
  shape: bbox 0.1295 x 0.1295 x 0.002 mm, 3 faces (baked)
FEATURE [Part::Feature] Part__Feature146  label="part044"
  shape: bbox 2.59 x 4.598 x 0.94 mm, 6 faces (baked)
FEATURE [Part::Feature] Part__Feature147  label="part045"
  shape: bbox 0.304 x 0.508 x 0.051 mm, 6 faces (baked)
FEATURE [Part::Feature] Part__Feature148  label="part046"
  shape: bbox 0.508 x 0.304 x 0.051 mm, 6 faces (baked)
FEATURE [Part::Feature] Part__Feature149  label="part047"
  shape: bbox 0.508 x 0.304 x 0.051 mm, 6 faces (baked)
FEATURE [Part::Feature] Part__Feature150  label="part048"
  shape: bbox 0.508 x 0.304 x 0.051 mm, 6 faces (baked)
FEATURE [Part::Feature] Part__Feature151  label="part049"
  shape: bbox 0.508 x 0.304 x 0.051 mm, 6 faces (baked)
FEATURE [Part::Feature] Part__Feature152  label="part050"
  shape: bbox 0.508 x 0.304 x 0.051 mm, 6 faces (baked)
FEATURE [Part::Feature] Part__Feature153  label="part051"
  shape: bbox 0.508 x 0.304 x 0.051 mm, 6 faces (baked)
FEATURE [Part::Feature] Part__Feature154  label="part052"
  shape: bbox 0.508 x 0.304 x 0.051 mm, 6 faces (baked)
FEATURE [Part::Feature] Part__Feature155  label="part053"
  shape: bbox 0.508 x 0.304 x 0.051 mm, 6 faces (baked)
FEATURE [Part::Feature] Part__Feature156  label="part054"
  shape: bbox 0.304 x 0.508 x 0.051 mm, 6 faces (baked)
FEATURE [Part::Feature] Part__Feature157  label="part055"
  shape: bbox 0.304 x 0.508 x 0.051 mm, 6 faces (baked)
FEATURE [Part::Feature] Part__Feature158  label="part056"
  shape: bbox 0.508 x 0.304 x 0.051 mm, 6 faces (baked)
FEATURE [Part::Feature] Part__Feature159  label="part057"
  shape: bbox 0.508 x 0.304 x 0.051 mm, 6 faces (baked)
FEATURE [Part::Feature] Part__Feature160  label="part058"
  shape: bbox 0.508 x 0.304 x 0.051 mm, 6 faces (baked)
FEATURE [Part::Feature] Part__Feature161  label="part059"
  shape: bbox 0.508 x 0.304 x 0.051 mm, 6 faces (baked)
FEATURE [Part::Feature] Part__Feature162  label="part060"
  shape: bbox 0.508 x 0.304 x 0.051 mm, 6 faces (baked)
FEATURE [Part::Feature] Part__Feature163  label="part061"
  shape: bbox 0.508 x 0.304 x 0.051 mm, 6 faces (baked)
FEATURE [Part::Feature] Part__Feature164  label="part062"
  shape: bbox 0.508 x 0.304 x 0.051 mm, 6 faces (baked)
FEATURE [Part::Feature] Part__Feature165  label="part063"
  shape: bbox 0.508 x 0.304 x 0.051 mm, 6 faces (baked)
FEATURE [Part::Feature] Part__Feature166  label="part064"
  shape: bbox 0.304 x 0.508 x 0.051 mm, 6 faces (baked)
FEATURE [Part::Feature] Part__Feature167  label="part065"
  shape: bbox 1.144 x 3.15 x 0.051 mm, 6 faces (baked)
FEATURE [App::Part] part001  label="09_AdapVoltajeDigital.kicad_sch_part066_f10ad10a87d3"
  Group = -> [Part__Feature145,Part__Feature146,Part__Feature147,Part__Feature148,Part__Feature149,Part__Feature150,Part__Feature151,Part__Feature152,Part__Feature153,Part__Feature154,Part__Feature155,Part__Feature156,Part__Feature157,Part__Feature158,Part__Feature159,Part__Feature160,Part__Feature161,Part__Feature162,Part__Feature163,Part__Feature164,Part__Feature165,Part__Feature166,Part__Feature167]
  Origin = -> Origin021
  Placement = pos=(115.705,-131.35,-1.6) rot=(0.707107,0.707107,0;3.14159rad)
FEATURE [App::Link] _7_SensorTemperatura_kicad_sch_C_0805_2012Metric_4f3bec8a4ad3_ln_007  label="02_Amplificacion.kicad_sch_SensorTemperatura.kicad_sch_C_0805_2012Metric_774f6370d5cd"
  LinkPlacement = pos=(86.7003,-102.819,-1.6) rot=(0.707107,-0.707107,0;3.14159rad)
  LinkedObject = -> Shape001
  Placement = pos=(86.7003,-102.819,-1.6) rot=(0.707107,-0.707107,0;3.14159rad)
FEATURE [Part::Feature] Part__Feature168  label="part066"
  shape: bbox 0.2045 x 0.2045 x 0.002 mm, 3 faces (baked)
FEATURE [Part::Feature] Part__Feature169  label="part067"
  shape: bbox 4.09 x 4.09 x 0.762 mm, 6 faces (baked)
FEATURE [Part::Feature] Part__Feature170  label="part068"
  shape: bbox 0.661 x 0.356 x 0.051 mm, 6 faces (baked)
FEATURE [Part::Feature] Part__Feature171  label="part069"
  shape: bbox 0.661 x 0.356 x 0.051 mm, 6 faces (baked)
FEATURE [Part::Feature] Part__Feature172  label="part070"
  shape: bbox 0.661 x 0.356 x 0.051 mm, 6 faces (baked)
FEATURE [Part::Feature] Part__Feature173  label="part071"
  shape: bbox 0.356 x 0.661 x 0.051 mm, 6 faces (baked)
FEATURE [Part::Feature] Part__Feature174  label="part072"
  shape: bbox 0.356 x 0.661 x 0.051 mm, 6 faces (baked)
FEATURE [Part::Feature] Part__Feature175  label="part073"
  shape: bbox 0.356 x 0.661 x 0.051 mm, 6 faces (baked)
FEATURE [Part::Feature] Part__Feature176  label="part074"
  shape: bbox 0.661 x 0.356 x 0.051 mm, 6 faces (baked)
FEATURE [Part::Feature] Part__Feature177  label="part075"
  shape: bbox 0.661 x 0.356 x 0.051 mm, 6 faces (baked)
FEATURE [Part::Feature] Part__Feature178  label="part076"
  shape: bbox 0.661 x 0.356 x 0.051 mm, 6 faces (baked)
FEATURE [Part::Feature] Part__Feature179  label="part077"
  shape: bbox 0.356 x 0.661 x 0.051 mm, 6 faces (baked)
FEATURE [Part::Feature] Part__Feature180  label="part078"
  shape: bbox 0.356 x 0.661 x 0.051 mm, 6 faces (baked)
FEATURE [Part::Feature] Part__Feature181  label="part079"
  shape: bbox 0.356 x 0.661 x 0.051 mm, 6 faces (baked)
FEATURE [Part::Feature] Part__Feature182  label="part080"
  shape: bbox 2.26 x 2.26 x 0.051 mm, 6 faces (baked)
FEATURE [App::Part] part002  label="01_Polarizacion.kicad_sch_part081_0638eee03de4"
  Group = -> [Part__Feature168,Part__Feature169,Part__Feature170,Part__Feature171,Part__Feature172,Part__Feature173,Part__Feature174,Part__Feature175,Part__Feature176,Part__Feature177,Part__Feature178,Part__Feature179,Part__Feature180,Part__Feature181,Part__Feature182]
  Origin = -> Origin022
  Placement = pos=(77.1605,-122.725,-1.6) rot=(1,0,0;3.14159rad)
FEATURE [App::Link] _7_SensorTemperatura_kicad_sch_C_0805_2012Metric_4f3bec8a4ad3_ln_008  label="05_ExtensionPulso.kicad_sch_SensorTemperatura.kicad_sch_C_0805_2012Metric_75119aad0e11"
  LinkPlacement = pos=(76.95,-84.5962,-1.6) rot=(0.707107,-0.707107,0;3.14159rad)
  LinkedObject = -> Shape001
  Placement = pos=(76.95,-84.5962,-1.6) rot=(0.707107,-0.707107,0;3.14159rad)
FEATURE [App::Link] _7_SensorTemperatura_kicad_sch_C_0805_2012Metric_4f3bec8a4ad3_ln_009  label="04_GenVref.kicad_sch_SensorTemperatura.kicad_sch_C_0805_2012Metric_bcff3c3a8cb2"
  LinkPlacement = pos=(126.65,-100.518,-1.6) rot=(0.707107,-0.707107,0;3.14159rad)
  LinkedObject = -> Shape001
  Placement = pos=(126.65,-100.518,-1.6) rot=(0.707107,-0.707107,0;3.14159rad)
FEATURE [Part::Feature] Part__Feature183  label="BODY-SON"
  Placement = pos=(0,0,0.025) rot=(1,0,0;1.5708rad)
  shape: bbox 2 x 2 x 0.75 mm, 59 faces (baked)
FEATURE [Part::Feature] Part__Feature184  label="SOLID"
  shape: bbox 1.1 x 0.2 x 2 mm, 28 faces (baked)
FEATURE [Part::Feature] Part__Feature185  label="SOLID001"
  shape: bbox 0.3 x 0.2 x 0.25 mm, 6 faces (baked)
FEATURE [Part::Feature] Part__Feature186  label="SOLID002"
  shape: bbox 0.3 x 0.2 x 0.25 mm, 6 faces (baked)
FEATURE [Part::Feature] Part__Feature187  label="SOLID003"
  shape: bbox 0.3 x 0.2 x 0.25 mm, 6 faces (baked)
FEATURE [Part::Feature] Part__Feature188  label="SOLID004"
  shape: bbox 0.3 x 0.2 x 0.25 mm, 6 faces (baked)
FEATURE [Part::Feature] Part__Feature189  label="SOLID005"
  shape: bbox 0.3 x 0.2 x 0.25 mm, 6 faces (baked)
FEATURE [Part::Feature] Part__Feature190  label="SOLID006"
  shape: bbox 0.3 x 0.2 x 0.25 mm, 6 faces (baked)
FEATURE [Part::Feature] Part__Feature191  label="SOLID007"
  shape: bbox 0.3 x 0.2 x 0.25 mm, 6 faces (baked)
FEATURE [Part::Feature] Part__Feature192  label="SOLID008"
  shape: bbox 0.3 x 0.2 x 0.25 mm, 6 faces (baked)
FEATURE [App::Part] FRAME_DSG0008A  label="FRAME-DSG0008A"
  Group = -> [Part__Feature184,Part__Feature185,Part__Feature186,Part__Feature187,Part__Feature188,Part__Feature189,Part__Feature190,Part__Feature191,Part__Feature192]
  Origin = -> Origin023
  Placement = pos=(0,0,0) rot=(1,0,0;1.5708rad)
FEATURE [App::Part] DSG0008A_ASM  label="02_Amplificacion.kicad_sch_DSG0008A_ASM_57f97972f78b"
  Group = -> [Part__Feature183,FRAME_DSG0008A]
  Origin = -> Origin024
  Placement = pos=(83.5001,-106.472,-1.6) rot=(0.707107,0.707107,0;3.14159rad)
FEATURE [App::Link] _7_SensorTemperatura_kicad_sch_C_0805_2012Metric_4f3bec8a4ad3_ln_010  label="04_GenVref.kicad_sch_SensorTemperatura.kicad_sch_C_0805_2012Metric_2e55c9e9e7a3"
  LinkPlacement = pos=(125.55,-94.718,-1.6) rot=(0.707107,-0.707107,0;3.14159rad)
  LinkedObject = -> Shape001
  Placement = pos=(125.55,-94.718,-1.6) rot=(0.707107,-0.707107,0;3.14159rad)
FEATURE [App::Link] _4_GenVref_kicad_sch_R_0805_2012Metric_e7e7c0ed52a6_ln_011  label="05_ExtensionPulso.kicad_sch_GenVref.kicad_sch_R_0805_2012Metric_d70c889e8c59"
  LinkPlacement = pos=(103.763,-95.9788,-1.6) rot=(1,0,0;3.14159rad)
  LinkedObject = -> Shape003
  Placement = pos=(103.763,-95.9788,-1.6) rot=(1,0,0;3.14159rad)
FEATURE [Part::Feature] Part__Feature193  label="part081"
  shape: bbox 0.1499 x 0.1499 x 0.002 mm, 3 faces (baked)
FEATURE [Part::Feature] Part__Feature194  label="part082"
  shape: bbox 2.998 x 2.998 x 0.889 mm, 6 faces (baked)
FEATURE [Part::Feature] Part__Feature195  label="part083"
  shape: bbox 1.6 x 2.412 x 0.051 mm, 6 faces (baked)
FEATURE [Part::Feature] Part__Feature196  label="part084"
  shape: bbox 0.559 x 0.356 x 0.47 mm, 8 faces (baked)
FEATURE [Part::Feature] Part__Feature197  label="part085"
  shape: bbox 0.559 x 0.356 x 0.47 mm, 8 faces (baked)
FEATURE [Part::Feature] Part__Feature198  label="part086"
  shape: bbox 0.559 x 0.356 x 0.47 mm, 8 faces (baked)
FEATURE [Part::Feature] Part__Feature199  label="part087"
  shape: bbox 0.559 x 0.356 x 0.47 mm, 8 faces (baked)
FEATURE [Part::Feature] Part__Feature200  label="part088"
  shape: bbox 0.559 x 0.356 x 0.47 mm, 8 faces (baked)
FEATURE [Part::Feature] Part__Feature201  label="part089"
  shape: bbox 0.559 x 0.356 x 0.47 mm, 8 faces (baked)
FEATURE [Part::Feature] Part__Feature202  label="part090"
  shape: bbox 0.559 x 0.356 x 0.47 mm, 8 faces (baked)
FEATURE [Part::Feature] Part__Feature203  label="part091"
  shape: bbox 0.559 x 0.356 x 0.47 mm, 8 faces (baked)
FEATURE [App::Part] part003  label="04_GenVref.kicad_sch_part092_94bb9f3815f2"
  Group = -> [Part__Feature193,Part__Feature194,Part__Feature195,Part__Feature196,Part__Feature197,Part__Feature198,Part__Feature199,Part__Feature200,Part__Feature201,Part__Feature202,Part__Feature203]
  Origin = -> Origin025
  Placement = pos=(123.775,-100.84,-1.6) rot=(0.707107,0.707107,0;3.14159rad)
FEATURE [App::Link] _1_Polarizacion_kicad_sch_C_0603_1608Metric_c67edd4d6b6e_ln_  label="01_Polarizacion.kicad_sch_Polarizacion.kicad_sch_C_0603_1608Metric_377d0d437d72"
  LinkPlacement = pos=(93.675,-122.6,-1.6) rot=(0.707107,-0.707107,0;3.14159rad)
  LinkedObject = -> Shape007
  Placement = pos=(93.675,-122.6,-1.6) rot=(0.707107,-0.707107,0;3.14159rad)
FEATURE [Part::Feature] Part__Feature204  label="part092"
  shape: bbox 0.06985 x 0.06985 x 0.003 mm, 3 faces (baked)
FEATURE [Part::Feature] Part__Feature205  label="part093"
  shape: bbox 1.397 x 2.161 x 1.093 mm, 14 faces (baked)
FEATURE [Part::Feature] Part__Feature206  label="part094"
  shape: bbox 0.498 x 0.306 x 0.675 mm, 14 faces (baked)
FEATURE [Part::Feature] Part__Feature207  label="part095"
  shape: bbox 0.498 x 0.306 x 0.675 mm, 14 faces (baked)
FEATURE [Part::Feature] Part__Feature208  label="part096"
  shape: bbox 0.498 x 0.306 x 0.675 mm, 14 faces (baked)
FEATURE [Part::Feature] Part__Feature209  label="part097"
  shape: bbox 0.498 x 0.306 x 0.675 mm, 14 faces (baked)
FEATURE [Part::Feature] Part__Feature210  label="part098"
  shape: bbox 0.498 x 0.306 x 0.675 mm, 14 faces (baked)
FEATURE [App::Part] part004  label="05_ExtensionPulso.kicad_sch_part099_1e18ba8c7ab6"
  Group = -> [Part__Feature204,Part__Feature205,Part__Feature206,Part__Feature207,Part__Feature208,Part__Feature209,Part__Feature210]
  Origin = -> Origin026
  Placement = pos=(72.6,-89.4674,-1.6) rot=(0.707107,-0.707107,0;3.14159rad)
FEATURE [App::Link] _4_GenVref_kicad_sch_R_0805_2012Metric_e7e7c0ed52a6_ln_012  label="09_AdapVoltajeDigital.kicad_sch_GenVref.kicad_sch_R_0805_2012Metric_22443eea2ec5"
  LinkPlacement = pos=(63.6875,-86.2086,-1.6) rot=(0,1,0;3.14159rad)
  LinkedObject = -> Shape003
  Placement = pos=(63.6875,-86.2086,-1.6) rot=(0,1,0;3.14159rad)
FEATURE [App::Link] _9_AdapVoltajeDigital_kicad_sch_part066_f10ad10a87d3_ln_  label="09_AdapVoltajeDigital.kicad_sch_AdapVoltajeDigital.kicad_sch_part066_6fb70bc1b834"
  LinkPlacement = pos=(64.525,-81,-1.6) rot=(0.707107,-0.707107,0;3.14159rad)
  LinkedObject = -> part001
  Placement = pos=(64.525,-81,-1.6) rot=(0.707107,-0.707107,0;3.14159rad)
FEATURE [App::Link] _4_GenVref_kicad_sch_R_0805_2012Metric_e7e7c0ed52a6_ln_013  label="03_Comparación.kicad_sch_GenVref.kicad_sch_R_0805_2012Metric_3096b1cac325"
  LinkPlacement = pos=(92.2717,-88.4092,-1.6) rot=(0.707107,0.707107,0;3.14159rad)
  LinkedObject = -> Shape003
  Placement = pos=(92.2717,-88.4092,-1.6) rot=(0.707107,0.707107,0;3.14159rad)
FEATURE [App::Link] _7_SensorTemperatura_kicad_sch_C_0805_2012Metric_4f3bec8a4ad3_ln_011  label="09_AdapVoltajeDigital.kicad_sch_SensorTemperatura.kicad_sch_C_0805_2012Metric_b93b06797fd4"
  LinkPlacement = pos=(60.425,-85.65,-1.6) rot=(0.707107,-0.707107,0;3.14159rad)
  LinkedObject = -> Shape001
  Placement = pos=(60.425,-85.65,-1.6) rot=(0.707107,-0.707107,0;3.14159rad)
FEATURE [App::Link] _1_Polarizacion_kicad_sch_R_0603_1608Metric_55dffa615082_ln_  label="01_Polarizacion.kicad_sch_Polarizacion.kicad_sch_R_0603_1608Metric_87d748e844b2"
  LinkPlacement = pos=(71.725,-124.5,-1.6) rot=(0.707107,0.707107,0;3.14159rad)
  LinkedObject = -> Shape004
  Placement = pos=(71.725,-124.5,-1.6) rot=(0.707107,0.707107,0;3.14159rad)
FEATURE [App::Link] _7_SensorTemperatura_kicad_sch_C_0805_2012Metric_4f3bec8a4ad3_ln_012  label="09_AdapVoltajeDigital.kicad_sch_SensorTemperatura.kicad_sch_C_0805_2012Metric_7cd32f02eb0c"
  LinkPlacement = pos=(120.4,-132.3,-1.6) rot=(1,0,0;3.14159rad)
  LinkedObject = -> Shape001
  Placement = pos=(120.4,-132.3,-1.6) rot=(1,0,0;3.14159rad)
FEATURE [Part::Feature] Part__Feature211  label="part099"
  shape: bbox 0.108 x 0.108 x 0.002 mm, 3 faces (baked)
FEATURE [Part::Feature] Part__Feature212  label="part100"
  shape: bbox 2.16 x 2.16 x 0.559 mm, 6 faces (baked)
FEATURE [Part::Feature] Part__Feature213  label="part101"
  shape: bbox 0.458 x 1.6 x 0.051 mm, 6 faces (baked)
FEATURE [Part::Feature] Part__Feature214  label="part102"
  shape: bbox 0.432 x 0.304 x 0.305 mm, 8 faces (baked)
FEATURE [Part::Feature] Part__Feature215  label="part103"
  shape: bbox 0.432 x 0.304 x 0.305 mm, 8 faces (baked)
FEATURE [Part::Feature] Part__Feature216  label="part104"
  shape: bbox 0.432 x 0.304 x 0.305 mm, 8 faces (baked)
FEATURE [Part::Feature] Part__Feature217  label="part105"
  shape: bbox 0.432 x 0.304 x 0.305 mm, 8 faces (baked)
FEATURE [Part::Feature] Part__Feature218  label="part106"
  shape: bbox 0.432 x 0.304 x 0.305 mm, 8 faces (baked)
FEATURE [Part::Feature] Part__Feature219  label="part107"
  shape: bbox 0.432 x 0.304 x 0.305 mm, 8 faces (baked)
FEATURE [Part::Feature] Part__Feature220  label="part108"
  shape: bbox 0.432 x 0.304 x 0.305 mm, 8 faces (baked)
FEATURE [Part::Feature] Part__Feature221  label="part109"
  shape: bbox 0.432 x 0.304 x 0.305 mm, 8 faces (baked)
FEATURE [App::Part] part005  label="04_GenVref.kicad_sch_part110_0b65658de655"
  Group = -> [Part__Feature211,Part__Feature212,Part__Feature213,Part__Feature214,Part__Feature215,Part__Feature216,Part__Feature217,Part__Feature218,Part__Feature219,Part__Feature220,Part__Feature221]
  Origin = -> Origin027
  Placement = pos=(60.666,-116.7,-1.6) rot=(0,1,0;3.14159rad)
FEATURE [App::Link] _7_SensorTemperatura_kicad_sch_C_0805_2012Metric_4f3bec8a4ad3_ln_013  label="05_ExtensionPulso.kicad_sch_SensorTemperatura.kicad_sch_C_0805_2012Metric_16ae6ca4e98c"
  LinkPlacement = pos=(75,-80.8462,-1.6) rot=(0,1,0;3.14159rad)
  LinkedObject = -> Shape001
  Placement = pos=(75,-80.8462,-1.6) rot=(0,1,0;3.14159rad)
FEATURE [App::Link] _1_Polarizacion_kicad_sch_R_0603_1608Metric_55dffa615082_ln_001  label="01_Polarizacion.kicad_sch_Polarizacion.kicad_sch_R_0603_1608Metric_5b352e1b5e06"
  LinkPlacement = pos=(74.075,-132.3,-1.6) rot=(1,0,0;3.14159rad)
  LinkedObject = -> Shape004
  Placement = pos=(74.075,-132.3,-1.6) rot=(1,0,0;3.14159rad)
FEATURE [App::Link] _7_SensorTemperatura_kicad_sch_C_0805_2012Metric_4f3bec8a4ad3_ln_014  label="08_MedicionCorriente.kicad_sch_SensorTemperatura.kicad_sch_C_0805_2012Metric_8dee5ab16994"
  LinkPlacement = pos=(121.325,-90.8,-1.6) rot=(1,0,0;3.14159rad)
  LinkedObject = -> Shape001
  Placement = pos=(121.325,-90.8,-1.6) rot=(1,0,0;3.14159rad)
FEATURE [App::Link] _1_Polarizacion_kicad_sch_part081_0638eee03de4_ln_  label="01_Polarizacion.kicad_sch_Polarizacion.kicad_sch_part081_9e2737b78b34"
  LinkPlacement = pos=(100.911,-120.825,-1.6) rot=(1,0,0;3.14159rad)
  LinkedObject = -> part002
  Placement = pos=(100.911,-120.825,-1.6) rot=(1,0,0;3.14159rad)
FEATURE [App::Link] _7_SensorTemperatura_kicad_sch_C_0805_2012Metric_4f3bec8a4ad3_ln_015  label="04_GenVref.kicad_sch_SensorTemperatura.kicad_sch_C_0805_2012Metric_5886e44a3407"
  LinkPlacement = pos=(60.7,-114.2,-1.6) rot=(1,0,0;3.14159rad)
  LinkedObject = -> Shape001
  Placement = pos=(60.7,-114.2,-1.6) rot=(1,0,0;3.14159rad)
FEATURE [App::Link] _4_GenVref_kicad_sch_R_0805_2012Metric_e7e7c0ed52a6_ln_014  label="03_Comparación.kicad_sch_GenVref.kicad_sch_R_0805_2012Metric_3270b82b8e41"
  LinkPlacement = pos=(96.2842,-92.9217,-1.6) rot=(0,1,0;3.14159rad)
  LinkedObject = -> Shape003
  Placement = pos=(96.2842,-92.9217,-1.6) rot=(0,1,0;3.14159rad)
FEATURE [App::Link] _4_GenVref_kicad_sch_R_0805_2012Metric_e7e7c0ed52a6_ln_015  label="03_Comparación.kicad_sch_GenVref.kicad_sch_R_0805_2012Metric_33ee9d32e46a"
  LinkPlacement = pos=(83.4,-98.3,-1.6) rot=(0.707107,0.707107,0;3.14159rad)
  LinkedObject = -> Shape003
  Placement = pos=(83.4,-98.3,-1.6) rot=(0.707107,0.707107,0;3.14159rad)
FEATURE [App::Link] _7_SensorTemperatura_kicad_sch_C_0805_2012Metric_4f3bec8a4ad3_ln_016  label="01_Polarizacion.kicad_sch_SensorTemperatura.kicad_sch_C_0805_2012Metric_723fa919f4c1"
  LinkPlacement = pos=(78.8,-136.95,-1.6) rot=(1,0,0;3.14159rad)
  LinkedObject = -> Shape001
  Placement = pos=(78.8,-136.95,-1.6) rot=(1,0,0;3.14159rad)
FEATURE [App::Link] _1_Polarizacion_kicad_sch_MUA08A_ASM_555f9891b5ac_ln_  label="01_Polarizacion.kicad_sch_Polarizacion.kicad_sch_MUA08A_ASM_e9cd949d0871"
  LinkPlacement = pos=(101.787,-132.225,-1.6) rot=(1,0,0;3.14159rad)
  LinkedObject = -> MUA08A_ASM
  Placement = pos=(101.787,-132.225,-1.6) rot=(1,0,0;3.14159rad)
FEATURE [App::Link] _4_GenVref_kicad_sch_R_0805_2012Metric_e7e7c0ed52a6_ln_016  label="03_Comparación.kicad_sch_GenVref.kicad_sch_R_0805_2012Metric_6877350ee7a3"
  LinkPlacement = pos=(82.25,-92.8592,-1.6) rot=(0.707107,0.707107,0;3.14159rad)
  LinkedObject = -> Shape003
  Placement = pos=(82.25,-92.8592,-1.6) rot=(0.707107,0.707107,0;3.14159rad)
FEATURE [Part::Feature] Part__Feature222  label="part110"
  shape: bbox 0.1029 x 0.1029 x 0.002 mm, 3 faces (baked)
FEATURE [Part::Feature] Part__Feature223  label="part111"
  shape: bbox 2.058 x 2.058 x 0.762 mm, 6 faces (baked)
FEATURE [Part::Feature] Part__Feature224  label="part112"
  shape: bbox 0.99 x 1.702 x 0.051 mm, 6 faces (baked)
FEATURE [Part::Feature] Part__Feature225  label="part113"
  shape: bbox 0.356 x 0.304 x 0.406 mm, 8 faces (baked)
FEATURE [Part::Feature] Part__Feature226  label="part114"
  shape: bbox 0.356 x 0.304 x 0.406 mm, 8 faces (baked)
FEATURE [Part::Feature] Part__Feature227  label="part115"
  shape: bbox 0.356 x 0.304 x 0.406 mm, 8 faces (baked)
FEATURE [Part::Feature] Part__Feature228  label="part116"
  shape: bbox 0.356 x 0.304 x 0.406 mm, 8 faces (baked)
FEATURE [Part::Feature] Part__Feature229  label="part117"
  shape: bbox 0.356 x 0.304 x 0.406 mm, 8 faces (baked)
FEATURE [Part::Feature] Part__Feature230  label="part118"
  shape: bbox 0.356 x 0.304 x 0.406 mm, 8 faces (baked)
FEATURE [Part::Feature] Part__Feature231  label="part119"
  shape: bbox 0.356 x 0.304 x 0.406 mm, 8 faces (baked)
FEATURE [Part::Feature] Part__Feature232  label="part120"
  shape: bbox 0.356 x 0.304 x 0.406 mm, 8 faces (baked)
FEATURE [App::Part] part006  label="03_Comparación.kicad_sch_part121_1eafd4a0765f"
  Group = -> [Part__Feature222,Part__Feature223,Part__Feature224,Part__Feature225,Part__Feature226,Part__Feature227,Part__Feature228,Part__Feature229,Part__Feature230,Part__Feature231,Part__Feature232]
  Origin = -> Origin028
  Placement = pos=(94.7217,-90.025,-1.6) rot=(0.707107,0.707107,0;3.14159rad)
FEATURE [App::Link] _4_GenVref_kicad_sch_R_0805_2012Metric_e7e7c0ed52a6_ln_017  label="04_GenVref.kicad_sch_GenVref.kicad_sch_R_0805_2012Metric_ad12786016aa"
  LinkPlacement = pos=(64.05,-116.438,-1.6) rot=(0.707107,-0.707107,0;3.14159rad)
  LinkedObject = -> Shape003
  Placement = pos=(64.05,-116.438,-1.6) rot=(0.707107,-0.707107,0;3.14159rad)
FEATURE [App::Link] _4_GenVref_kicad_sch_R_0805_2012Metric_e7e7c0ed52a6_ln_018  label="04_GenVref.kicad_sch_GenVref.kicad_sch_R_0805_2012Metric_82f41cffb9c5"
  LinkPlacement = pos=(61.0625,-119.2,-1.6) rot=(0,1,0;3.14159rad)
  LinkedObject = -> Shape003
  Placement = pos=(61.0625,-119.2,-1.6) rot=(0,1,0;3.14159rad)
FEATURE [App::Link] _1_Polarizacion_kicad_sch_R_0603_1608Metric_55dffa615082_ln_002  label="01_Polarizacion.kicad_sch_Polarizacion.kicad_sch_R_0603_1608Metric_1f6309ed5df5"
  LinkPlacement = pos=(82.125,-120.675,-1.6) rot=(1,0,0;3.14159rad)
  LinkedObject = -> Shape004
  Placement = pos=(82.125,-120.675,-1.6) rot=(1,0,0;3.14159rad)
FEATURE [App::Link] _4_GenVref_kicad_sch_R_0805_2012Metric_e7e7c0ed52a6_ln_019  label="08_MedicionCorriente.kicad_sch_GenVref.kicad_sch_R_0805_2012Metric_42b8563f0a1e"
  LinkPlacement = pos=(65.3147,-92.6719,-1.6) rot=(0.707107,0.707107,0;3.14159rad)
  LinkedObject = -> Shape003
  Placement = pos=(65.3147,-92.6719,-1.6) rot=(0.707107,0.707107,0;3.14159rad)
FEATURE [App::Link] _7_SensorTemperatura_kicad_sch_C_0805_2012Metric_4f3bec8a4ad3_ln_017  label="08_MedicionCorriente.kicad_sch_SensorTemperatura.kicad_sch_C_0805_2012Metric_d9559b3a91d4"
  LinkPlacement = pos=(54.8147,-101.009,-1.6) rot=(0.707107,-0.707107,0;3.14159rad)
  LinkedObject = -> Shape001
  Placement = pos=(54.8147,-101.009,-1.6) rot=(0.707107,-0.707107,0;3.14159rad)
FEATURE [App::Link] _4_GenVref_kicad_sch_R_0805_2012Metric_e7e7c0ed52a6_ln_020  label="09_AdapVoltajeDigital.kicad_sch_GenVref.kicad_sch_R_0805_2012Metric_fc7e7ce7e395"
  LinkPlacement = pos=(63.6875,-84.0086,-1.6) rot=(0,1,0;3.14159rad)
  LinkedObject = -> Shape003
  Placement = pos=(63.6875,-84.0086,-1.6) rot=(0,1,0;3.14159rad)
FEATURE [App::Link] _7_SensorTemperatura_kicad_sch_C_0805_2012Metric_4f3bec8a4ad3_ln_018  label="01_Polarizacion.kicad_sch_SensorTemperatura.kicad_sch_C_0805_2012Metric_cce1ed306186"
  LinkPlacement = pos=(71.15,-114.4,-1.6) rot=(1,0,0;3.14159rad)
  LinkedObject = -> Shape001
  Placement = pos=(71.15,-114.4,-1.6) rot=(1,0,0;3.14159rad)
FEATURE [App::Link] _7_SensorTemperatura_kicad_sch_C_0805_2012Metric_4f3bec8a4ad3_ln_019  label="03_Comparación.kicad_sch_SensorTemperatura.kicad_sch_C_0805_2012Metric_dd3db2bc50c2"
  LinkPlacement = pos=(85,-91.5717,-1.6) rot=(0,1,0;3.14159rad)
  LinkedObject = -> Shape001
  Placement = pos=(85,-91.5717,-1.6) rot=(0,1,0;3.14159rad)
FEATURE [App::Link] _4_GenVref_kicad_sch_R_0805_2012Metric_e7e7c0ed52a6_ln_021  label="01_Polarizacion.kicad_sch_GenVref.kicad_sch_R_0805_2012Metric_b5629ff8e78c"
  LinkPlacement = pos=(90.7,-120.85,-1.6) rot=(1,0,0;3.14159rad)
  LinkedObject = -> Shape003
  Placement = pos=(90.7,-120.85,-1.6) rot=(1,0,0;3.14159rad)
FEATURE [App::Link] _4_GenVref_kicad_sch_R_0805_2012Metric_e7e7c0ed52a6_ln_022  label="09_AdapVoltajeDigital.kicad_sch_GenVref.kicad_sch_R_0805_2012Metric_a5ce9ec5bd63"
  LinkPlacement = pos=(68.575,-80.9211,-1.6) rot=(0.707107,0.707107,0;3.14159rad)
  LinkedObject = -> Shape003
  Placement = pos=(68.575,-80.9211,-1.6) rot=(0.707107,0.707107,0;3.14159rad)
FEATURE [App::Link] _1_Polarizacion_kicad_sch_R_0603_1608Metric_55dffa615082_ln_003  label="01_Polarizacion.kicad_sch_Polarizacion.kicad_sch_R_0603_1608Metric_f878bf51fab8"
  LinkPlacement = pos=(95.475,-122.6,-1.6) rot=(0.707107,0.707107,0;3.14159rad)
  LinkedObject = -> Shape004
  Placement = pos=(95.475,-122.6,-1.6) rot=(0.707107,0.707107,0;3.14159rad)
FEATURE [App::Link] _4_GenVref_kicad_sch_R_0805_2012Metric_e7e7c0ed52a6_ln_023  label="09_AdapVoltajeDigital.kicad_sch_GenVref.kicad_sch_R_0805_2012Metric_5d58ee5fd994"
  LinkPlacement = pos=(111.55,-131.338,-1.6) rot=(0.707107,0.707107,0;3.14159rad)
  LinkedObject = -> Shape003
  Placement = pos=(111.55,-131.338,-1.6) rot=(0.707107,0.707107,0;3.14159rad)
FEATURE [App::Link] _7_SensorTemperatura_kicad_sch_C_0805_2012Metric_4f3bec8a4ad3_ln_020  label="03_Comparación.kicad_sch_SensorTemperatura.kicad_sch_C_0805_2012Metric_bea9cc050107"
  LinkPlacement = pos=(96.2217,-95.0217,-1.6) rot=(1,0,0;3.14159rad)
  LinkedObject = -> Shape001
  Placement = pos=(96.2217,-95.0217,-1.6) rot=(1,0,0;3.14159rad)
FEATURE [App::Link] _4_GenVref_kicad_sch_R_0805_2012Metric_e7e7c0ed52a6_ln_024  label="08_MedicionCorriente.kicad_sch_GenVref.kicad_sch_R_0805_2012Metric_8813cbe12152"
  LinkPlacement = pos=(57.4147,-106.447,-1.6) rot=(0.707107,-0.707107,0;3.14159rad)
  LinkedObject = -> Shape003
  Placement = pos=(57.4147,-106.447,-1.6) rot=(0.707107,-0.707107,0;3.14159rad)
FEATURE [App::Link] _4_GenVref_kicad_sch_part110_0b65658de655_ln_  label="08_MedicionCorriente.kicad_sch_GenVref.kicad_sch_part110_745eed0a042c"
  LinkPlacement = pos=(58.95,-94.216,-1.6) rot=(1,0,0;3.14159rad)
  LinkedObject = -> part005
  Placement = pos=(58.95,-94.216,-1.6) rot=(1,0,0;3.14159rad)
FEATURE [App::Link] _4_GenVref_kicad_sch_R_0805_2012Metric_e7e7c0ed52a6_ln_025  label="03_Comparación.kicad_sch_GenVref.kicad_sch_R_0805_2012Metric_7cc34fb34ed2"
  LinkPlacement = pos=(86.2625,-97.3717,-1.6) rot=(0,1,0;3.14159rad)
  LinkedObject = -> Shape003
  Placement = pos=(86.2625,-97.3717,-1.6) rot=(0,1,0;3.14159rad)
FEATURE [App::Link] _4_GenVref_kicad_sch_R_0805_2012Metric_e7e7c0ed52a6_ln_026  label="02_Amplificacion.kicad_sch_GenVref.kicad_sch_R_0805_2012Metric_a60f9344c819"
  LinkPlacement = pos=(80.3003,-109.919,-1.6) rot=(0,1,0;3.14159rad)
  LinkedObject = -> Shape003
  Placement = pos=(80.3003,-109.919,-1.6) rot=(0,1,0;3.14159rad)
FEATURE [App::Link] _1_Polarizacion_kicad_sch_C_0603_1608Metric_c67edd4d6b6e_ln_001  label="01_Polarizacion.kicad_sch_Polarizacion.kicad_sch_C_0603_1608Metric_8734bcb53b1a"
  LinkPlacement = pos=(69.925,-124.5,-1.6) rot=(0.707107,-0.707107,0;3.14159rad)
  LinkedObject = -> Shape007
  Placement = pos=(69.925,-124.5,-1.6) rot=(0.707107,-0.707107,0;3.14159rad)
FEATURE [App::Link] _4_GenVref_kicad_sch_R_0805_2012Metric_e7e7c0ed52a6_ln_027  label="02_Amplificacion.kicad_sch_GenVref.kicad_sch_R_0805_2012Metric_7dccb3957ba2"
  LinkPlacement = pos=(84.3003,-112.769,-1.6) rot=(1,0,0;3.14159rad)
  LinkedObject = -> Shape003
  Placement = pos=(84.3003,-112.769,-1.6) rot=(1,0,0;3.14159rad)
FEATURE [App::Link] _5_ExtensionPulso_kicad_sch_part099_1e18ba8c7ab6_ln_  label="05_ExtensionPulso.kicad_sch_ExtensionPulso.kicad_sch_part099_c91216c64a90"
  LinkPlacement = pos=(106.2,-85.2576,-1.6) rot=(0.707107,0.707107,0;3.14159rad)
  LinkedObject = -> part004
  Placement = pos=(106.2,-85.2576,-1.6) rot=(0.707107,0.707107,0;3.14159rad)
FEATURE [App::Link] _1_Polarizacion_kicad_sch_R_0603_1608Metric_55dffa615082_ln_004  label="01_Polarizacion.kicad_sch_Polarizacion.kicad_sch_R_0603_1608Metric_908aef1b5755"
  LinkPlacement = pos=(98.675,-115.35,-1.6) rot=(0.707107,0.707107,0;3.14159rad)
  LinkedObject = -> Shape004
  Placement = pos=(98.675,-115.35,-1.6) rot=(0.707107,0.707107,0;3.14159rad)
FEATURE [Part::Feature] Part__Feature233  label="SOT765 Mold body"
  Placement = pos=(-0.0103397,0.90197,2.80263) rot=(0,0,1;0rad)
  shape: bbox 2.002 x 0.725 x 2.302 mm, 69 faces (baked)
FEATURE [Part::Feature] Part__Feature234  label="SOT765 Lead"
  Placement = pos=(0.34966,0.827142,3.20263) rot=(0,-1,0;1.5708rad)
  shape: bbox 0.22 x 0.56 x 0.4395 mm, 12 faces (baked)
FEATURE [Part::Feature] Part__Feature235  label="SOT765 Lead001"
  Placement = pos=(0.84966,0.827142,3.20263) rot=(0,-1,0;1.5708rad)
  shape: bbox 0.22 x 0.56 x 0.4395 mm, 12 faces (baked)
FEATURE [Part::Feature] Part__Feature236  label="SOT765 Lead002"
  Placement = pos=(1.34966,0.827142,3.20263) rot=(0,-1,0;1.5708rad)
  shape: bbox 0.22 x 0.56 x 0.4395 mm, 12 faces (baked)
FEATURE [Part::Feature] Part__Feature237  label="SOT765 Lead003"
  Placement = pos=(1.84966,0.827142,3.20263) rot=(0,-1,0;1.5708rad)
  shape: bbox 0.22 x 0.56 x 0.4395 mm, 12 faces (baked)
FEATURE [Part::Feature] Part__Feature238  label="SOT765 Lead004"
  Placement = pos=(1.62966,0.827142,0.102631) rot=(0,1,0;1.5708rad)
  shape: bbox 0.22 x 0.56 x 0.4395 mm, 12 faces (baked)
FEATURE [Part::Feature] Part__Feature239  label="SOT765 Lead005"
  Placement = pos=(1.12966,0.827142,0.102631) rot=(0,1,0;1.5708rad)
  shape: bbox 0.22 x 0.56 x 0.4395 mm, 12 faces (baked)
FEATURE [Part::Feature] Part__Feature240  label="SOT765 Lead006"
  Placement = pos=(0.62966,0.827142,0.102631) rot=(0,1,0;1.5708rad)
  shape: bbox 0.22 x 0.56 x 0.4395 mm, 12 faces (baked)
FEATURE [Part::Feature] Part__Feature241  label="SOT765 Lead007"
  Placement = pos=(0.12966,0.827142,0.102631) rot=(0,1,0;1.5708rad)
  shape: bbox 0.22 x 0.56 x 0.4395 mm, 12 faces (baked)
FEATURE [App::Part] SOT765_1  label="05_ExtensionPulso.kicad_sch_SOT765-1_c610b25eeb40"
  Group = -> [Part__Feature233,Part__Feature234,Part__Feature235,Part__Feature236,Part__Feature237,Part__Feature238,Part__Feature239,Part__Feature240,Part__Feature241]
  Origin = -> Origin029
  Placement = pos=(103.75,-91.7288,-0.8) rot=(-1,0,0;1.5708rad)
FEATURE [App::Link] _4_GenVref_kicad_sch_R_0805_2012Metric_e7e7c0ed52a6_ln_028  label="08_MedicionCorriente.kicad_sch_GenVref.kicad_sch_R_0805_2012Metric_a1aa6a97c580"
  LinkPlacement = pos=(126.763,-88.2,-1.6) rot=(1,0,0;3.14159rad)
  LinkedObject = -> Shape003
  Placement = pos=(126.763,-88.2,-1.6) rot=(1,0,0;3.14159rad)
FEATURE [App::Link] _1_Polarizacion_kicad_sch_R_0603_1608Metric_55dffa615082_ln_005  label="01_Polarizacion.kicad_sch_Polarizacion.kicad_sch_R_0603_1608Metric_d50ca8de9c10"
  LinkPlacement = pos=(105.875,-118.775,-1.6) rot=(1,0,0;3.14159rad)
  LinkedObject = -> Shape004
  Placement = pos=(105.875,-118.775,-1.6) rot=(1,0,0;3.14159rad)
FEATURE [App::Link] _7_SensorTemperatura_kicad_sch_C_0805_2012Metric_4f3bec8a4ad3_ln_021  label="01_Polarizacion.kicad_sch_SensorTemperatura.kicad_sch_C_0805_2012Metric_9fcbaec610d1"
  LinkPlacement = pos=(101.8,-135.1,-1.6) rot=(1,0,0;3.14159rad)
  LinkedObject = -> Shape001
  Placement = pos=(101.8,-135.1,-1.6) rot=(1,0,0;3.14159rad)
FEATURE [App::Link] _4_GenVref_kicad_sch_R_0805_2012Metric_e7e7c0ed52a6_ln_029  label="05_ExtensionPulso.kicad_sch_GenVref.kicad_sch_R_0805_2012Metric_02d44a6916a2"
  LinkPlacement = pos=(73.35,-92.3462,-1.6) rot=(1,0,0;3.14159rad)
  LinkedObject = -> Shape003
  Placement = pos=(73.35,-92.3462,-1.6) rot=(1,0,0;3.14159rad)
FEATURE [App::Link] _7_SensorTemperatura_kicad_sch_C_0805_2012Metric_4f3bec8a4ad3_ln_022  label="02_Amplificacion.kicad_sch_SensorTemperatura.kicad_sch_C_0805_2012Metric_da0146491d4e"
  LinkPlacement = pos=(94.7751,-102.093,-1.6) rot=(1,0,0;3.14159rad)
  LinkedObject = -> Shape001
  Placement = pos=(94.7751,-102.093,-1.6) rot=(1,0,0;3.14159rad)
FEATURE [App::Link] _7_SensorTemperatura_kicad_sch_C_0805_2012Metric_4f3bec8a4ad3_ln_023  label="03_Comparación.kicad_sch_SensorTemperatura.kicad_sch_C_0805_2012Metric_a4d24e94fc1b"
  LinkPlacement = pos=(86.2,-99.4717,-1.6) rot=(1,0,0;3.14159rad)
  LinkedObject = -> Shape001
  Placement = pos=(86.2,-99.4717,-1.6) rot=(1,0,0;3.14159rad)
FEATURE [App::Link] _4_GenVref_kicad_sch_R_0805_2012Metric_e7e7c0ed52a6_ln_030  label="01_Polarizacion.kicad_sch_GenVref.kicad_sch_R_0805_2012Metric_9b28d168cab5"
  LinkPlacement = pos=(67.65,-120.013,-1.6) rot=(0.707107,-0.707107,0;3.14159rad)
  LinkedObject = -> Shape003
  Placement = pos=(67.65,-120.013,-1.6) rot=(0.707107,-0.707107,0;3.14159rad)
FEATURE [App::Link] _4_GenVref_kicad_sch_part110_0b65658de655_ln_001  label="04_GenVref.kicad_sch_GenVref.kicad_sch_part110_1d7efe95acaf"
  LinkPlacement = pos=(123,-94.784,-1.6) rot=(0.707107,0.707107,0;3.14159rad)
  LinkedObject = -> part005
  Placement = pos=(123,-94.784,-1.6) rot=(0.707107,0.707107,0;3.14159rad)
FEATURE [App::Link] _1_Polarizacion_kicad_sch_C_1206_3216Metric_f1471ee13c61_ln_  label="01_Polarizacion.kicad_sch_Polarizacion.kicad_sch_C_1206_3216Metric_c440844d8f1a"
  LinkPlacement = pos=(106.75,-120.775,-1.6) rot=(0,1,0;3.14159rad)
  LinkedObject = -> Shape005
  Placement = pos=(106.75,-120.775,-1.6) rot=(0,1,0;3.14159rad)
FEATURE [App::Link] _7_SensorTemperatura_kicad_sch_C_0805_2012Metric_4f3bec8a4ad3_ln_024  label="02_Amplificacion.kicad_sch_SensorTemperatura.kicad_sch_C_0805_2012Metric_022299c087be"
  LinkPlacement = pos=(102.1,-111.1,-1.6) rot=(0,1,0;3.14159rad)
  LinkedObject = -> Shape001
  Placement = pos=(102.1,-111.1,-1.6) rot=(0,1,0;3.14159rad)
FEATURE [App::Link] _4_GenVref_kicad_sch_R_0805_2012Metric_e7e7c0ed52a6_ln_031  label="08_MedicionCorriente.kicad_sch_GenVref.kicad_sch_R_0805_2012Metric_88afb1e3a43c"
  LinkPlacement = pos=(112.987,-80.3,-1.6) rot=(0,1,0;3.14159rad)
  LinkedObject = -> Shape003
  Placement = pos=(112.987,-80.3,-1.6) rot=(0,1,0;3.14159rad)
FEATURE [App::Link] _4_GenVref_kicad_sch_R_0805_2012Metric_e7e7c0ed52a6_ln_032  label="02_Amplificacion.kicad_sch_GenVref.kicad_sch_R_0805_2012Metric_e6567e01b36d"
  LinkPlacement = pos=(94.7926,-100.063,-1.6) rot=(1,0,0;3.14159rad)
  LinkedObject = -> Shape003
  Placement = pos=(94.7926,-100.063,-1.6) rot=(1,0,0;3.14159rad)
FEATURE [App::Link] _1_Polarizacion_kicad_sch_D_SOD_123_c84daf4213db_ln_  label="01_Polarizacion.kicad_sch_Polarizacion.kicad_sch_D_SOD_123_cfec7389e37c"
  LinkPlacement = pos=(75.275,-128.675,-1.6) rot=(1,0,0;3.14159rad)
  LinkedObject = -> Shape006
  Placement = pos=(75.275,-128.675,-1.6) rot=(1,0,0;3.14159rad)
FEATURE [App::Link] _7_SensorTemperatura_kicad_sch_C_0805_2012Metric_4f3bec8a4ad3_ln_025  label="02_Amplificacion.kicad_sch_SensorTemperatura.kicad_sch_C_0805_2012Metric_65447a7f0012"
  LinkPlacement = pos=(84.3003,-114.769,-1.6) rot=(1,0,0;3.14159rad)
  LinkedObject = -> Shape001
  Placement = pos=(84.3003,-114.769,-1.6) rot=(1,0,0;3.14159rad)
FEATURE [App::Link] _4_GenVref_kicad_sch_R_0805_2012Metric_e7e7c0ed52a6_ln_033  label="06_PlacasSiPM.kicad_sch_GenVref.kicad_sch_R_0805_2012Metric_b0d47a4007dc"
  LinkPlacement = pos=(53.7,-87.2125,-1.6) rot=(0.707107,0.707107,0;3.14159rad)
  LinkedObject = -> Shape003
  Placement = pos=(53.7,-87.2125,-1.6) rot=(0.707107,0.707107,0;3.14159rad)
FEATURE [App::Link] _7_SensorTemperatura_kicad_sch_C_0805_2012Metric_4f3bec8a4ad3_ln_026  label="09_AdapVoltajeDigital.kicad_sch_SensorTemperatura.kicad_sch_C_0805_2012Metric_558a5019f77a"
  LinkPlacement = pos=(120.4,-130.309,-1.6) rot=(1,0,0;3.14159rad)
  LinkedObject = -> Shape001
  Placement = pos=(120.4,-130.309,-1.6) rot=(1,0,0;3.14159rad)
FEATURE [App::Link] _7_SensorTemperatura_kicad_sch_C_0805_2012Metric_4f3bec8a4ad3_ln_027  label="01_Polarizacion.kicad_sch_SensorTemperatura.kicad_sch_C_0805_2012Metric_79b9d7ec9f46"
  LinkPlacement = pos=(75.3,-136.95,-1.6) rot=(0,1,0;3.14159rad)
  LinkedObject = -> Shape001
  Placement = pos=(75.3,-136.95,-1.6) rot=(0,1,0;3.14159rad)
FEATURE [App::Link] _4_GenVref_kicad_sch_R_0805_2012Metric_e7e7c0ed52a6_ln_034  label="08_MedicionCorriente.kicad_sch_GenVref.kicad_sch_R_0805_2012Metric_1c1c66d6041b"
  LinkPlacement = pos=(54.4147,-97.0594,-1.6) rot=(1,0,0;3.14159rad)
  LinkedObject = -> Shape003
  Placement = pos=(54.4147,-97.0594,-1.6) rot=(1,0,0;3.14159rad)
FEATURE [App::Link] _1_Polarizacion_kicad_sch_C_0603_1608Metric_c67edd4d6b6e_ln_002  label="01_Polarizacion.kicad_sch_Polarizacion.kicad_sch_C_0603_1608Metric_01af951ef0cc"
  LinkPlacement = pos=(71.725,-127.9,-1.6) rot=(0.707107,-0.707107,0;3.14159rad)
  LinkedObject = -> Shape007
  Placement = pos=(71.725,-127.9,-1.6) rot=(0.707107,-0.707107,0;3.14159rad)
FEATURE [App::Link] _7_SensorTemperatura_kicad_sch_C_0805_2012Metric_4f3bec8a4ad3_ln_028  label="02_Amplificacion.kicad_sch_SensorTemperatura.kicad_sch_C_0805_2012Metric_d0fc4e760fa5"
  LinkPlacement = pos=(94.8,-110.25,-1.6) rot=(1,0,0;3.14159rad)
  LinkedObject = -> Shape001
  Placement = pos=(94.8,-110.25,-1.6) rot=(1,0,0;3.14159rad)
FEATURE [App::Link] _4_GenVref_kicad_sch_R_0805_2012Metric_e7e7c0ed52a6_ln_035  label="02_Amplificacion.kicad_sch_GenVref.kicad_sch_R_0805_2012Metric_5a66527fed67"
  LinkPlacement = pos=(98.35,-101.95,-1.6) rot=(1,0,0;3.14159rad)
  LinkedObject = -> Shape003
  Placement = pos=(98.35,-101.95,-1.6) rot=(1,0,0;3.14159rad)
FEATURE [App::Link] _7_SensorTemperatura_kicad_sch_C_0805_2012Metric_4f3bec8a4ad3_ln_029  label="09_AdapVoltajeDigital.kicad_sch_SensorTemperatura.kicad_sch_C_0805_2012Metric_716435be677b"
  LinkPlacement = pos=(60.625,-76.9,-1.6) rot=(0.707107,-0.707107,0;3.14159rad)
  LinkedObject = -> Shape001
  Placement = pos=(60.625,-76.9,-1.6) rot=(0.707107,-0.707107,0;3.14159rad)
FEATURE [App::Link] _7_SensorTemperatura_kicad_sch_C_0805_2012Metric_4f3bec8a4ad3_ln_030  label="02_Amplificacion.kicad_sch_SensorTemperatura.kicad_sch_C_0805_2012Metric_b87bbd415e4b"
  LinkPlacement = pos=(86.0503,-106.369,-1.6) rot=(0.707107,-0.707107,0;3.14159rad)
  LinkedObject = -> Shape001
  Placement = pos=(86.0503,-106.369,-1.6) rot=(0.707107,-0.707107,0;3.14159rad)
FEATURE [App::Link] _7_SensorTemperatura_kicad_sch_C_0805_2012Metric_4f3bec8a4ad3_ln_031  label="02_Amplificacion.kicad_sch_SensorTemperatura.kicad_sch_C_0805_2012Metric_bf15bd18cb4c"
  LinkPlacement = pos=(100.2,-99.9,-1.6) rot=(0,1,0;3.14159rad)
  LinkedObject = -> Shape001
  Placement = pos=(100.2,-99.9,-1.6) rot=(0,1,0;3.14159rad)
FEATURE [App::Link] _4_GenVref_kicad_sch_R_0805_2012Metric_e7e7c0ed52a6_ln_036  label="04_GenVref.kicad_sch_GenVref.kicad_sch_R_0805_2012Metric_e13380c9df2f"
  LinkPlacement = pos=(57.85,-114.737,-1.6) rot=(0.707107,-0.707107,0;3.14159rad)
  LinkedObject = -> Shape003
  Placement = pos=(57.85,-114.737,-1.6) rot=(0.707107,-0.707107,0;3.14159rad)
FEATURE [App::Link] _1_Polarizacion_kicad_sch_part043_50eeabfdbd3f_ln_  label="04_GenVref.kicad_sch_Polarizacion.kicad_sch_part043_c88fd473e1c9"
  LinkPlacement = pos=(118.596,-101.277,-1.6) rot=(0.707107,-0.707107,0;3.14159rad)
  LinkedObject = -> part
  Placement = pos=(118.596,-101.277,-1.6) rot=(0.707107,-0.707107,0;3.14159rad)
FEATURE [App::Link] _1_Polarizacion_kicad_sch_C_1206_3216Metric_f1471ee13c61_ln_001  label="01_Polarizacion.kicad_sch_Polarizacion.kicad_sch_C_1206_3216Metric_0792a4aa511d"
  LinkPlacement = pos=(83,-122.675,-1.6) rot=(0,1,0;3.14159rad)
  LinkedObject = -> Shape005
  Placement = pos=(83,-122.675,-1.6) rot=(0,1,0;3.14159rad)
FEATURE [App::Link] _4_GenVref_kicad_sch_R_0805_2012Metric_e7e7c0ed52a6_ln_037  label="08_MedicionCorriente.kicad_sch_GenVref.kicad_sch_R_0805_2012Metric_1bc3f010a1d9"
  LinkPlacement = pos=(54.8147,-93.8719,-1.6) rot=(0.707107,0.707107,0;3.14159rad)
  LinkedObject = -> Shape003
  Placement = pos=(54.8147,-93.8719,-1.6) rot=(0.707107,0.707107,0;3.14159rad)
FEATURE [App::Link] _1_Polarizacion_kicad_sch_R_0603_1608Metric_55dffa615082_ln_006  label="01_Polarizacion.kicad_sch_Polarizacion.kicad_sch_R_0603_1608Metric_b670a5560d47"
  LinkPlacement = pos=(101.9,-115.35,-1.6) rot=(0.707107,-0.707107,0;3.14159rad)
  LinkedObject = -> Shape004
  Placement = pos=(101.9,-115.35,-1.6) rot=(0.707107,-0.707107,0;3.14159rad)
FEATURE [App::Link] _4_GenVref_kicad_sch_R_0805_2012Metric_e7e7c0ed52a6_ln_038  label="02_Amplificacion.kicad_sch_GenVref.kicad_sch_R_0805_2012Metric_98ae2756dd18"
  LinkPlacement = pos=(80.3178,-105.849,-1.6) rot=(0,1,0;3.14159rad)
  LinkedObject = -> Shape003
  Placement = pos=(80.3178,-105.849,-1.6) rot=(0,1,0;3.14159rad)
FEATURE [App::Link] _4_GenVref_kicad_sch_R_0805_2012Metric_e7e7c0ed52a6_ln_039  label="02_Amplificacion.kicad_sch_GenVref.kicad_sch_R_0805_2012Metric_50dd63f23907"
  LinkPlacement = pos=(87.4503,-109.981,-1.6) rot=(0.707107,-0.707107,0;3.14159rad)
  LinkedObject = -> Shape003
  Placement = pos=(87.4503,-109.981,-1.6) rot=(0.707107,-0.707107,0;3.14159rad)
FEATURE [App::Link] _4_GenVref_kicad_sch_R_0805_2012Metric_e7e7c0ed52a6_ln_040  label="09_AdapVoltajeDigital.kicad_sch_GenVref.kicad_sch_R_0805_2012Metric_a94d198717ec"
  LinkPlacement = pos=(63.6625,-77.8086,-1.6) rot=(0,1,0;3.14159rad)
  LinkedObject = -> Shape003
  Placement = pos=(63.6625,-77.8086,-1.6) rot=(0,1,0;3.14159rad)
FEATURE [App::Link] _4_GenVref_kicad_sch_R_0805_2012Metric_e7e7c0ed52a6_ln_041  label="02_Amplificacion.kicad_sch_GenVref.kicad_sch_R_0805_2012Metric_9be5b2abd6fe"
  LinkPlacement = pos=(94.7926,-104.123,-1.6) rot=(0,1,0;3.14159rad)
  LinkedObject = -> Shape003
  Placement = pos=(94.7926,-104.123,-1.6) rot=(0,1,0;3.14159rad)
FEATURE [App::Link] _7_SensorTemperatura_kicad_sch_C_0805_2012Metric_4f3bec8a4ad3_ln_032  label="05_ExtensionPulso.kicad_sch_SensorTemperatura.kicad_sch_C_0805_2012Metric_58d80b1f3cd1"
  LinkPlacement = pos=(70.75,-85.7962,-1.6) rot=(0.707107,0.707107,0;3.14159rad)
  LinkedObject = -> Shape001
  Placement = pos=(70.75,-85.7962,-1.6) rot=(0.707107,0.707107,0;3.14159rad)
FEATURE [App::Link] _4_GenVref_kicad_sch_R_0805_2012Metric_e7e7c0ed52a6_ln_042  label="05_ExtensionPulso.kicad_sch_GenVref.kicad_sch_R_0805_2012Metric_b3f6f6ee3aee"
  LinkPlacement = pos=(105.45,-82.3788,-1.6) rot=(0,1,0;3.14159rad)
  LinkedObject = -> Shape003
  Placement = pos=(105.45,-82.3788,-1.6) rot=(0,1,0;3.14159rad)
FEATURE [App::Link] _4_GenVref_kicad_sch_R_0805_2012Metric_e7e7c0ed52a6_ln_043  label="05_ExtensionPulso.kicad_sch_GenVref.kicad_sch_R_0805_2012Metric_1f2b9ba4228d"
  LinkPlacement = pos=(73.3625,-94.3462,-1.6) rot=(1,0,0;3.14159rad)
  LinkedObject = -> Shape003
  Placement = pos=(73.3625,-94.3462,-1.6) rot=(1,0,0;3.14159rad)
FEATURE [App::Link] _3_Comparaci__n_kicad_sch_part121_1eafd4a0765f_ln_  label="03_Comparación.kicad_sch_Comparación.kicad_sch_part121_844a8964707b"
  LinkPlacement = pos=(84.7,-94.475,-1.6) rot=(0.707107,0.707107,0;3.14159rad)
  LinkedObject = -> part006
  Placement = pos=(84.7,-94.475,-1.6) rot=(0.707107,0.707107,0;3.14159rad)
FEATURE [App::Link] _4_GenVref_kicad_sch_R_0805_2012Metric_e7e7c0ed52a6_ln_044  label="01_Polarizacion.kicad_sch_GenVref.kicad_sch_R_0805_2012Metric_0eca787ff260"
  LinkPlacement = pos=(89.95,-123.6,-1.6) rot=(0.707107,0.707107,0;3.14159rad)
  LinkedObject = -> Shape003
  Placement = pos=(89.95,-123.6,-1.6) rot=(0.707107,0.707107,0;3.14159rad)
FEATURE [App::Link] _1_Polarizacion_kicad_sch_R_0603_1608Metric_55dffa615082_ln_007  label="01_Polarizacion.kicad_sch_Polarizacion.kicad_sch_R_0603_1608Metric_b9c7bb0d40c0"
  LinkPlacement = pos=(74.925,-117.25,-1.6) rot=(0.707107,0.707107,0;3.14159rad)
  LinkedObject = -> Shape004
  Placement = pos=(74.925,-117.25,-1.6) rot=(0.707107,0.707107,0;3.14159rad)
FEATURE [App::Link] _2_Amplificacion_kicad_sch_DSG0008A_ASM_57f97972f78b_ln_  label="02_Amplificacion.kicad_sch_Amplificacion.kicad_sch_DSG0008A_ASM_f97134277b03"
  LinkPlacement = pos=(97.9998,-104.753,-1.6) rot=(0.707107,0.707107,0;3.14159rad)
  LinkedObject = -> DSG0008A_ASM
  Placement = pos=(97.9998,-104.753,-1.6) rot=(0.707107,0.707107,0;3.14159rad)
FEATURE [App::Link] _4_GenVref_kicad_sch_R_0805_2012Metric_e7e7c0ed52a6_ln_045  label="02_Amplificacion.kicad_sch_GenVref.kicad_sch_R_0805_2012Metric_b4c80ec9a720"
  LinkPlacement = pos=(101.95,-108.263,-1.6) rot=(0.707107,-0.707107,0;3.14159rad)
  LinkedObject = -> Shape003
  Placement = pos=(101.95,-108.263,-1.6) rot=(0.707107,-0.707107,0;3.14159rad)
FEATURE [App::Link] _4_GenVref_kicad_sch_R_0805_2012Metric_e7e7c0ed52a6_ln_046  label="05_ExtensionPulso.kicad_sch_GenVref.kicad_sch_R_0805_2012Metric_300720f2948e"
  LinkPlacement = pos=(105.438,-80.3788,-1.6) rot=(0,1,0;3.14159rad)
  LinkedObject = -> Shape003
  Placement = pos=(105.438,-80.3788,-1.6) rot=(0,1,0;3.14159rad)
FEATURE [App::Link] _7_SensorTemperatura_kicad_sch_C_0805_2012Metric_4f3bec8a4ad3_ln_033  label="05_ExtensionPulso.kicad_sch_SensorTemperatura.kicad_sch_C_0805_2012Metric_6b9403680f9f"
  LinkPlacement = pos=(108.05,-88.9288,-1.6) rot=(0.707107,-0.707107,0;3.14159rad)
  LinkedObject = -> Shape001
  Placement = pos=(108.05,-88.9288,-1.6) rot=(0.707107,-0.707107,0;3.14159rad)
FEATURE [App::Link] _1_Polarizacion_kicad_sch_C_1206_3216Metric_f1471ee13c61_ln_002  label="01_Polarizacion.kicad_sch_Polarizacion.kicad_sch_C_1206_3216Metric_29e822de8fbe"
  LinkPlacement = pos=(71.65,-116.875,-1.6) rot=(1,0,0;3.14159rad)
  LinkedObject = -> Shape005
  Placement = pos=(71.65,-116.875,-1.6) rot=(1,0,0;3.14159rad)
FEATURE [App::Link] _7_SensorTemperatura_kicad_sch_C_0805_2012Metric_4f3bec8a4ad3_ln_034  label="02_Amplificacion.kicad_sch_SensorTemperatura.kicad_sch_C_0805_2012Metric_95746ad1d714"
  LinkPlacement = pos=(85.4503,-110.019,-1.6) rot=(0.707107,0.707107,0;3.14159rad)
  LinkedObject = -> Shape001
  Placement = pos=(85.4503,-110.019,-1.6) rot=(0.707107,0.707107,0;3.14159rad)
FEATURE [Part::Feature] Shape009  label="01_Polarizacion.kicad_sch_L_1812_4532Metric_baccccf5fdc4"
  Placement = pos=(107.075,-124.912,-1.6) rot=(0.707107,-0.707107,0;3.14159rad)
  shape: bbox 3.2 x 4.5 x 2.5 mm, 28 faces (baked)
FEATURE [App::Link] _1_Polarizacion_kicad_sch_R_0603_1608Metric_55dffa615082_ln_008  label="01_Polarizacion.kicad_sch_Polarizacion.kicad_sch_R_0603_1608Metric_38d55a5e51e8"
  LinkPlacement = pos=(107.3,-129.35,-1.6) rot=(1,0,0;3.14159rad)
  LinkedObject = -> Shape004
  Placement = pos=(107.3,-129.35,-1.6) rot=(1,0,0;3.14159rad)
FEATURE [App::Link] _7_SensorTemperatura_kicad_sch_C_0805_2012Metric_4f3bec8a4ad3_ln_035  label="05_ExtensionPulso.kicad_sch_SensorTemperatura.kicad_sch_C_0805_2012Metric_5644b2da582a"
  LinkPlacement = pos=(101.85,-90.1288,-1.6) rot=(0.707107,0.707107,0;3.14159rad)
  LinkedObject = -> Shape001
  Placement = pos=(101.85,-90.1288,-1.6) rot=(0.707107,0.707107,0;3.14159rad)
FEATURE [App::Link] _4_GenVref_kicad_sch_R_0805_2012Metric_e7e7c0ed52a6_ln_047  label="05_ExtensionPulso.kicad_sch_GenVref.kicad_sch_R_0805_2012Metric_0b9095136ad4"
  LinkPlacement = pos=(75.0375,-78.7462,-1.6) rot=(0,1,0;3.14159rad)
  LinkedObject = -> Shape003
  Placement = pos=(75.0375,-78.7462,-1.6) rot=(0,1,0;3.14159rad)
FEATURE [Part::Feature] Part__Feature242  label="BODY-SO"
  Placement = pos=(0,0,1.0033) rot=(0.57735,0.57735,0.57735;2.0944rad)
  shape: bbox 3.915 x 4.906 x 1.451 mm, 56 faces (baked)
FEATURE [Part::Feature] Part__Feature243  label="LEAD-D0008A"
  Placement = pos=(2.159,1.905,0.254) rot=(0.57735,0.57735,0.57735;2.0944rad)
  shape: bbox 1.056 x 0.4071 x 1.004 mm, 13 faces (baked)
FEATURE [Part::Feature] Part__Feature244  label="LEAD-D0008A001"
  Placement = pos=(2.159,0.635,0.254) rot=(0.57735,0.57735,0.57735;2.0944rad)
  shape: bbox 1.056 x 0.4071 x 1.004 mm, 13 faces (baked)
FEATURE [Part::Feature] Part__Feature245  label="LEAD-D0008A002"
  Placement = pos=(2.159,-0.635,0.254) rot=(0.57735,0.57735,0.57735;2.0944rad)
  shape: bbox 1.056 x 0.4071 x 1.004 mm, 13 faces (baked)
FEATURE [Part::Feature] Part__Feature246  label="LEAD-D0008A003"
  Placement = pos=(2.159,-1.905,0.254) rot=(0.57735,0.57735,0.57735;2.0944rad)
  shape: bbox 1.056 x 0.4071 x 1.004 mm, 13 faces (baked)
FEATURE [Part::Feature] Part__Feature247  label="LEAD-D0008A004"
  Placement = pos=(-2.159,1.905,0.254) rot=(0.57735,-0.57735,-0.57735;2.0944rad)
  shape: bbox 1.056 x 0.4071 x 1.004 mm, 13 faces (baked)
FEATURE [Part::Feature] Part__Feature248  label="LEAD-D0008A005"
  Placement = pos=(-2.159,0.635,0.254) rot=(0.57735,-0.57735,-0.57735;2.0944rad)
  shape: bbox 1.056 x 0.4071 x 1.004 mm, 13 faces (baked)
FEATURE [Part::Feature] Part__Feature249  label="LEAD-D0008A006"
  Placement = pos=(-2.159,-0.635,0.254) rot=(0.57735,-0.57735,-0.57735;2.0944rad)
  shape: bbox 1.056 x 0.4071 x 1.004 mm, 13 faces (baked)
FEATURE [Part::Feature] Part__Feature250  label="LEAD-D0008A007"
  Placement = pos=(-2.159,-1.905,0.254) rot=(0.57735,-0.57735,-0.57735;2.0944rad)
  shape: bbox 1.056 x 0.4071 x 1.004 mm, 13 faces (baked)
FEATURE [App::Part] D0008A_ASM  label="08_MedicionCorriente.kicad_sch_D0008A_ASM_ff69cd2c6fd6"
  Group = -> [Part__Feature242,Part__Feature243,Part__Feature244,Part__Feature245,Part__Feature246,Part__Feature247,Part__Feature248,Part__Feature249,Part__Feature250]
  Origin = -> Origin030
  Placement = pos=(58.8097,-100.881,-1.6) rot=(0.707107,0.707107,0;3.14159rad)
FEATURE [App::Link] _7_SensorTemperatura_kicad_sch_C_0805_2012Metric_4f3bec8a4ad3_ln_036  label="03_Comparación.kicad_sch_SensorTemperatura.kicad_sch_C_0805_2012Metric_a5b05f6ce53c"
  LinkPlacement = pos=(95.0217,-87.1217,-1.6) rot=(0,1,0;3.14159rad)
  LinkedObject = -> Shape001
  Placement = pos=(95.0217,-87.1217,-1.6) rot=(0,1,0;3.14159rad)
FEATURE [App::Link] _4_GenVref_kicad_sch_R_0805_2012Metric_e7e7c0ed52a6_ln_048  label="02_Amplificacion.kicad_sch_GenVref.kicad_sch_R_0805_2012Metric_f350107516de"
  LinkPlacement = pos=(98.6375,-111.05,-1.6) rot=(1,0,0;3.14159rad)
  LinkedObject = -> Shape003
  Placement = pos=(98.6375,-111.05,-1.6) rot=(1,0,0;3.14159rad)
FEATURE [App::Link] _4_GenVref_kicad_sch_R_0805_2012Metric_e7e7c0ed52a6_ln_049  label="02_Amplificacion.kicad_sch_GenVref.kicad_sch_R_0805_2012Metric_bf8a3855538a"
  LinkPlacement = pos=(91.5,-93.75,-1.6) rot=(0.707107,0.707107,0;3.14159rad)
  LinkedObject = -> Shape003
  Placement = pos=(91.5,-93.75,-1.6) rot=(0.707107,0.707107,0;3.14159rad)
FEATURE [App::Link] _4_GenVref_kicad_sch_R_0805_2012Metric_e7e7c0ed52a6_ln_050  label="02_Amplificacion.kicad_sch_GenVref.kicad_sch_R_0805_2012Metric_7091d725528c"
  LinkPlacement = pos=(94.8,-108.2,-1.6) rot=(0,1,0;3.14159rad)
  LinkedObject = -> Shape003
  Placement = pos=(94.8,-108.2,-1.6) rot=(0,1,0;3.14159rad)
FEATURE [App::Link] _1_Polarizacion_kicad_sch_R_0603_1608Metric_55dffa615082_ln_009  label="01_Polarizacion.kicad_sch_Polarizacion.kicad_sch_R_0603_1608Metric_f64e8758f55e"
  LinkPlacement = pos=(100.275,-115.35,-1.6) rot=(0.707107,-0.707107,0;3.14159rad)
  LinkedObject = -> Shape004
  Placement = pos=(100.275,-115.35,-1.6) rot=(0.707107,-0.707107,0;3.14159rad)
FEATURE [App::Link] _4_GenVref_kicad_sch_R_0805_2012Metric_e7e7c0ed52a6_ln_051  label="02_Amplificacion.kicad_sch_GenVref.kicad_sch_R_0805_2012Metric_55ed9bbd2133"
  LinkPlacement = pos=(97.95,-108.3,-1.6) rot=(0.707107,-0.707107,0;3.14159rad)
  LinkedObject = -> Shape003
  Placement = pos=(97.95,-108.3,-1.6) rot=(0.707107,-0.707107,0;3.14159rad)
FEATURE [App::Link] _7_SensorTemperatura_kicad_sch_C_0805_2012Metric_4f3bec8a4ad3_ln_037  label="08_MedicionCorriente.kicad_sch_SensorTemperatura.kicad_sch_C_0805_2012Metric_2f8cfb197d40"
  LinkPlacement = pos=(117.275,-82.35,-1.6) rot=(0.707107,0.707107,0;3.14159rad)
  LinkedObject = -> Shape001
  Placement = pos=(117.275,-82.35,-1.6) rot=(0.707107,0.707107,0;3.14159rad)
FEATURE [App::Link] _7_SensorTemperatura_kicad_sch_C_0805_2012Metric_4f3bec8a4ad3_ln_038  label="02_Amplificacion.kicad_sch_SensorTemperatura.kicad_sch_C_0805_2012Metric_8fce02a2dac0"
  LinkPlacement = pos=(80.3003,-111.969,-1.6) rot=(1,0,0;3.14159rad)
  LinkedObject = -> Shape001
  Placement = pos=(80.3003,-111.969,-1.6) rot=(1,0,0;3.14159rad)
FEATURE [App::Link] _7_SensorTemperatura_kicad_sch_C_0805_2012Metric_4f3bec8a4ad3_ln_039  label="02_Amplificacion.kicad_sch_SensorTemperatura.kicad_sch_C_0805_2012Metric_646302445440"
  LinkPlacement = pos=(80.3003,-103.819,-1.6) rot=(1,0,0;3.14159rad)
  LinkedObject = -> Shape001
  Placement = pos=(80.3003,-103.819,-1.6) rot=(1,0,0;3.14159rad)
FEATURE [App::Link] _1_Polarizacion_kicad_sch_C_0603_1608Metric_c67edd4d6b6e_ln_003  label="01_Polarizacion.kicad_sch_Polarizacion.kicad_sch_C_0603_1608Metric_9a9a240c4004"
  LinkPlacement = pos=(95.475,-125.9,-1.6) rot=(0.707107,-0.707107,0;3.14159rad)
  LinkedObject = -> Shape007
  Placement = pos=(95.475,-125.9,-1.6) rot=(0.707107,-0.707107,0;3.14159rad)
FEATURE [App::Link] _7_SensorTemperatura_kicad_sch_C_0805_2012Metric_4f3bec8a4ad3_ln_040  label="05_ExtensionPulso.kicad_sch_SensorTemperatura.kicad_sch_C_0805_2012Metric_0fc7d2e462b8"
  LinkPlacement = pos=(103.8,-93.8788,-1.6) rot=(1,0,0;3.14159rad)
  LinkedObject = -> Shape001
  Placement = pos=(103.8,-93.8788,-1.6) rot=(1,0,0;3.14159rad)
FEATURE [App::Link] _1_Polarizacion_kicad_sch_L_1812_4532Metric_baccccf5fdc4_ln_  label="01_Polarizacion.kicad_sch_Polarizacion.kicad_sch_L_1812_4532Metric_8ad00610c4a7"
  LinkPlacement = pos=(83.325,-126.812,-1.6) rot=(0.707107,-0.707107,0;3.14159rad)
  LinkedObject = -> Shape009
  Placement = pos=(83.325,-126.812,-1.6) rot=(0.707107,-0.707107,0;3.14159rad)
FEATURE [App::Link] _7_SensorTemperatura_kicad_sch_C_0805_2012Metric_4f3bec8a4ad3_ln_041  label="02_Amplificacion.kicad_sch_SensorTemperatura.kicad_sch_C_0805_2012Metric_67048baeb127"
  LinkPlacement = pos=(94.7751,-106.143,-1.6) rot=(0,1,0;3.14159rad)
  LinkedObject = -> Shape001
  Placement = pos=(94.7751,-106.143,-1.6) rot=(0,1,0;3.14159rad)
FEATURE [App::Link] _7_SensorTemperatura_kicad_sch_C_0805_2012Metric_4f3bec8a4ad3_ln_042  label="02_Amplificacion.kicad_sch_SensorTemperatura.kicad_sch_C_0805_2012Metric_ccadb6048732"
  LinkPlacement = pos=(100.525,-104.643,-1.6) rot=(0.707107,-0.707107,0;3.14159rad)
  LinkedObject = -> Shape001
  Placement = pos=(100.525,-104.643,-1.6) rot=(0.707107,-0.707107,0;3.14159rad)
FEATURE [App::Link] _4_GenVref_kicad_sch_R_0805_2012Metric_e7e7c0ed52a6_ln_052  label="08_MedicionCorriente.kicad_sch_GenVref.kicad_sch_R_0805_2012Metric_aea0ff9fd0cc"
  LinkPlacement = pos=(112.988,-82.3,-1.6) rot=(1,0,0;3.14159rad)
  LinkedObject = -> Shape003
  Placement = pos=(112.988,-82.3,-1.6) rot=(1,0,0;3.14159rad)
FEATURE [App::Link] _8_MedicionCorriente_kicad_sch_D0008A_ASM_ff69cd2c6fd6_ln_  label="08_MedicionCorriente.kicad_sch_MedicionCorriente.kicad_sch_D0008A_ASM_2e8fd4a02845"
  LinkPlacement = pos=(121.196,-86.805,-1.6) rot=(0,1,0;3.14159rad)
  LinkedObject = -> D0008A_ASM
  Placement = pos=(121.196,-86.805,-1.6) rot=(0,1,0;3.14159rad)
FEATURE [App::Link] _1_Polarizacion_kicad_sch_C_0603_1608Metric_c67edd4d6b6e_ln_004  label="01_Polarizacion.kicad_sch_Polarizacion.kicad_sch_C_0603_1608Metric_284aad9b0a60"
  LinkPlacement = pos=(82.15,-119.075,-1.6) rot=(1,0,0;3.14159rad)
  LinkedObject = -> Shape007
  Placement = pos=(82.15,-119.075,-1.6) rot=(1,0,0;3.14159rad)
FEATURE [App::Link] _4_GenVref_kicad_sch_R_0805_2012Metric_e7e7c0ed52a6_ln_053  label="08_MedicionCorriente.kicad_sch_GenVref.kicad_sch_R_0805_2012Metric_e71e07bc5ef5"
  LinkPlacement = pos=(114.188,-90.8,-1.6) rot=(0,1,0;3.14159rad)
  LinkedObject = -> Shape003
  Placement = pos=(114.188,-90.8,-1.6) rot=(0,1,0;3.14159rad)
FEATURE [App::Link] _1_Polarizacion_kicad_sch_R_0603_1608Metric_55dffa615082_ln_010  label="01_Polarizacion.kicad_sch_Polarizacion.kicad_sch_R_0603_1608Metric_4167547f1817"
  LinkPlacement = pos=(107.3,-130.85,-1.6) rot=(0,1,0;3.14159rad)
  LinkedObject = -> Shape004
  Placement = pos=(107.3,-130.85,-1.6) rot=(0,1,0;3.14159rad)
FEATURE [App::Link] _7_SensorTemperatura_kicad_sch_C_0805_2012Metric_4f3bec8a4ad3_ln_043  label="02_Amplificacion.kicad_sch_SensorTemperatura.kicad_sch_C_0805_2012Metric_2a1fcab318d0"
  LinkPlacement = pos=(99.95,-108.3,-1.6) rot=(0.707107,0.707107,0;3.14159rad)
  LinkedObject = -> Shape001
  Placement = pos=(99.95,-108.3,-1.6) rot=(0.707107,0.707107,0;3.14159rad)
FEATURE [App::Link] _4_GenVref_kicad_sch_R_0805_2012Metric_e7e7c0ed52a6_ln_054  label="04_GenVref.kicad_sch_GenVref.kicad_sch_R_0805_2012Metric_9e7fd4aff466"
  LinkPlacement = pos=(53.7625,-118.35,-1.6) rot=(0,1,0;3.14159rad)
  LinkedObject = -> Shape003
  Placement = pos=(53.7625,-118.35,-1.6) rot=(0,1,0;3.14159rad)
FEATURE [App::Link] _4_GenVref_kicad_sch_R_0805_2012Metric_e7e7c0ed52a6_ln_055  label="05_ExtensionPulso.kicad_sch_GenVref.kicad_sch_R_0805_2012Metric_1bfc9547bef9"
  LinkPlacement = pos=(102.437,-86.1788,-1.6) rot=(1,0,0;3.14159rad)
  LinkedObject = -> Shape003
  Placement = pos=(102.437,-86.1788,-1.6) rot=(1,0,0;3.14159rad)
FEATURE [App::Link] _1_Polarizacion_kicad_sch_TSOT_23_32137845036f_ln_  label="01_Polarizacion.kicad_sch_Polarizacion.kicad_sch_TSOT_23_31ac76a80dc4"
  LinkPlacement = pos=(79.525,-127.565,-1.6) rot=(0.707107,-0.707107,0;3.14159rad)
  LinkedObject = -> Shape002
  Placement = pos=(79.525,-127.565,-1.6) rot=(0.707107,-0.707107,0;3.14159rad)
FEATURE [App::Link] _4_GenVref_kicad_sch_R_0805_2012Metric_e7e7c0ed52a6_ln_056  label="09_AdapVoltajeDigital.kicad_sch_GenVref.kicad_sch_R_0805_2012Metric_c2bcc9662ca4"
  LinkPlacement = pos=(63.6625,-75.6086,-1.6) rot=(0,1,0;3.14159rad)
  LinkedObject = -> Shape003
  Placement = pos=(63.6625,-75.6086,-1.6) rot=(0,1,0;3.14159rad)
FEATURE [App::Link] _4_GenVref_kicad_sch_R_0805_2012Metric_e7e7c0ed52a6_ln_057  label="02_Amplificacion.kicad_sch_GenVref.kicad_sch_R_0805_2012Metric_4f690526bdd6"
  LinkPlacement = pos=(81.35,-98.3125,-1.6) rot=(0.707107,0.707107,0;3.14159rad)
  LinkedObject = -> Shape003
  Placement = pos=(81.35,-98.3125,-1.6) rot=(0.707107,0.707107,0;3.14159rad)
FEATURE [App::Link] _4_GenVref_kicad_sch_R_0805_2012Metric_e7e7c0ed52a6_ln_058  label="02_Amplificacion.kicad_sch_GenVref.kicad_sch_R_0805_2012Metric_d994b1cb332c"
  LinkPlacement = pos=(83.3503,-110.006,-1.6) rot=(0.707107,-0.707107,0;3.14159rad)
  LinkedObject = -> Shape003
  Placement = pos=(83.3503,-110.006,-1.6) rot=(0.707107,-0.707107,0;3.14159rad)
FEATURE [App::Link] _1_Polarizacion_kicad_sch_R_0603_1608Metric_55dffa615082_ln_011  label="01_Polarizacion.kicad_sch_Polarizacion.kicad_sch_R_0603_1608Metric_858ad7995ed0"
  LinkPlacement = pos=(74.075,-133.8,-1.6) rot=(0,1,0;3.14159rad)
  LinkedObject = -> Shape004
  Placement = pos=(74.075,-133.8,-1.6) rot=(0,1,0;3.14159rad)
FEATURE [App::Link] _1_Polarizacion_kicad_sch_R_0603_1608Metric_55dffa615082_ln_012  label="01_Polarizacion.kicad_sch_Polarizacion.kicad_sch_R_0603_1608Metric_04d059b3d32a"
  LinkPlacement = pos=(78.1,-117.25,-1.6) rot=(0.707107,-0.707107,0;3.14159rad)
  LinkedObject = -> Shape004
  Placement = pos=(78.1,-117.25,-1.6) rot=(0.707107,-0.707107,0;3.14159rad)
FEATURE [App::Link] _4_GenVref_kicad_sch_R_0805_2012Metric_e7e7c0ed52a6_ln_059  label="02_Amplificacion.kicad_sch_GenVref.kicad_sch_R_0805_2012Metric_0f4e1581d0de"
  LinkPlacement = pos=(83.9503,-103.519,-1.6) rot=(1,0,0;3.14159rad)
  LinkedObject = -> Shape003
  Placement = pos=(83.9503,-103.519,-1.6) rot=(1,0,0;3.14159rad)
FEATURE [App::Link] _4_GenVref_kicad_sch_part110_0b65658de655_ln_002  label="08_MedicionCorriente.kicad_sch_GenVref.kicad_sch_part110_338fcaf85ea3"
  LinkPlacement = pos=(114.525,-87.006,-1.6) rot=(0.707107,0.707107,0;3.14159rad)
  LinkedObject = -> part005
  Placement = pos=(114.525,-87.006,-1.6) rot=(0.707107,0.707107,0;3.14159rad)
FEATURE [App::Link] _1_Polarizacion_kicad_sch_L_1210_3225Metric_350fa5c3db90_ln_  label="01_Polarizacion.kicad_sch_Polarizacion.kicad_sch_L_1210_3225Metric_86b3767c6717"
  LinkPlacement = pos=(70.925,-120.475,-1.6) rot=(0.707107,0.707107,0;3.14159rad)
  LinkedObject = -> Shape008
  Placement = pos=(70.925,-120.475,-1.6) rot=(0.707107,0.707107,0;3.14159rad)
FEATURE [App::Link] _4_GenVref_kicad_sch_R_0805_2012Metric_e7e7c0ed52a6_ln_060  label="04_GenVref.kicad_sch_GenVref.kicad_sch_R_0805_2012Metric_c68ca7f52acd"
  LinkPlacement = pos=(119.216,-105.147,-1.6) rot=(0.707107,-0.707107,0;3.14159rad)
  LinkedObject = -> Shape003
  Placement = pos=(119.216,-105.147,-1.6) rot=(0.707107,-0.707107,0;3.14159rad)
FEATURE [App::Link] _5_ExtensionPulso_kicad_sch_SOT765_1_c610b25eeb40_ln_  label="05_ExtensionPulso.kicad_sch_ExtensionPulso.kicad_sch_SOT765-1_d179a5160022"
  LinkPlacement = pos=(75.05,-82.9962,-0.8) rot=(0,0.707107,-0.707107;3.14159rad)
  LinkedObject = -> SOT765_1
  Placement = pos=(75.05,-82.9962,-0.8) rot=(0,0.707107,-0.707107;3.14159rad)
FEATURE [App::Link] _7_SensorTemperatura_kicad_sch_C_0805_2012Metric_4f3bec8a4ad3_ln_044  label="01_Polarizacion.kicad_sch_SensorTemperatura.kicad_sch_C_0805_2012Metric_645ca0f632d5"
  LinkPlacement = pos=(94.15,-112.55,-1.6) rot=(1,0,0;3.14159rad)
  LinkedObject = -> Shape001
  Placement = pos=(94.15,-112.55,-1.6) rot=(1,0,0;3.14159rad)
FEATURE [App::Link] _4_GenVref_kicad_sch_R_0805_2012Metric_e7e7c0ed52a6_ln_061  label="01_Polarizacion.kicad_sch_GenVref.kicad_sch_R_0805_2012Metric_47c688d4b46b"
  LinkPlacement = pos=(64.1,-123.55,-1.6) rot=(0.707107,0.707107,0;3.14159rad)
  LinkedObject = -> Shape003
  Placement = pos=(64.1,-123.55,-1.6) rot=(0.707107,0.707107,0;3.14159rad)
FEATURE [App::Link] _1_Polarizacion_kicad_sch_part043_50eeabfdbd3f_ln_001  label="04_GenVref.kicad_sch_Polarizacion.kicad_sch_part043_459e301dedef"
  LinkPlacement = pos=(55.1925,-115.33,-1.6) rot=(0,1,0;3.14159rad)
  LinkedObject = -> part
  Placement = pos=(55.1925,-115.33,-1.6) rot=(0,1,0;3.14159rad)
FEATURE [App::Link] _4_GenVref_kicad_sch_R_0805_2012Metric_e7e7c0ed52a6_ln_062  label="05_ExtensionPulso.kicad_sch_GenVref.kicad_sch_R_0805_2012Metric_39d6778915a5"
  LinkPlacement = pos=(76.3625,-88.5462,-1.6) rot=(0,1,0;3.14159rad)
  LinkedObject = -> Shape003
  Placement = pos=(76.3625,-88.5462,-1.6) rot=(0,1,0;3.14159rad)
FEATURE [App::Part] Bot_d980
  Group = -> [Shape002,Shape003,Shape004,_4_GenVref_kicad_sch_R_0805_2012Metric_e7e7c0ed52a6_ln_,MUA08A_ASM,Shape005,_7_SensorTemperatura_kicad_sch_C_0805_2012Metric_4f3bec8a4ad3_ln_,_4_GenVref_kicad_sch_R_0805_2012Metric_e7e7c0ed52a6_ln_001,_4_GenVref_kicad_sch_R_0805_2012Metric_e7e7c0ed52a6_ln_002,_4_GenVref_kicad_sch_R_0805_2012Metric_e7e7c0ed52a6_ln_003,+155 more]
  Origin = -> Origin004
FEATURE [App::Part] Step_Models_d980
  Group = -> [Top_d980,Bot_d980]
  Origin = -> Origin002
FEATURE [Part::Feature] pads_area001  label="topPads_d980"
  Placement = pos=(0,0,0.02) rot=(0,0,1;0rad)
  shape: bbox 77 x 73.75 x 2e-07 mm, 325 faces, 0 solids (baked)
FEATURE [Part::Feature] Shape011  label="topTracks_d980"
  Placement = pos=(0,0,0.01) rot=(0,0,1;0rad)
  shape: bbox 74.7 x 70.02 x 2e-07 mm, 57 faces, 0 solids (baked)
FEATURE [Part::Feature] zones_area001  label="topZones_d980"
  Placement = pos=(0,0,0.01) rot=(0,0,1;0rad)
  shape: bbox 79.25 x 78.25 x 2e-07 mm, 2 faces, 0 solids (baked)
FEATURE [Part::Feature] pads_area003  label="botPads_d980"
  Placement = pos=(0,0,-1.62) rot=(0,0,1;0rad)
  shape: bbox 77 x 73.75 x 2e-07 mm, 789 faces, 0 solids (baked)
FEATURE [Part::Feature] Shape013  label="botTracks_d980"
  Placement = pos=(0,0,-1.61) rot=(0,0,1;0rad)
  shape: bbox 76 x 73.5 x 2e-07 mm, 257 faces, 0 solids (baked)
FEATURE [Part::Feature] zones_area003  label="botZones_d980"
  Placement = pos=(0,0,-1.61) rot=(0,0,1;0rad)
  shape: bbox 25.36 x 9.067 x 2e-07 mm, 4 faces, 0 solids (baked)
FEATURE [App::Part] Board_Geoms_d980
  Group = -> [Pcb_d980,PCB_Sketch_d980,pads_area001,Shape011,zones_area001,pads_area003,Shape013,zones_area003]
  Origin = -> Origin
FEATURE [App::Part] Board_d980  label="Placa_DetectorParticulas"
  Group = -> [Local_CS_d980,Board_Geoms_d980,Step_Models_d980]
  Origin = -> Origin001
